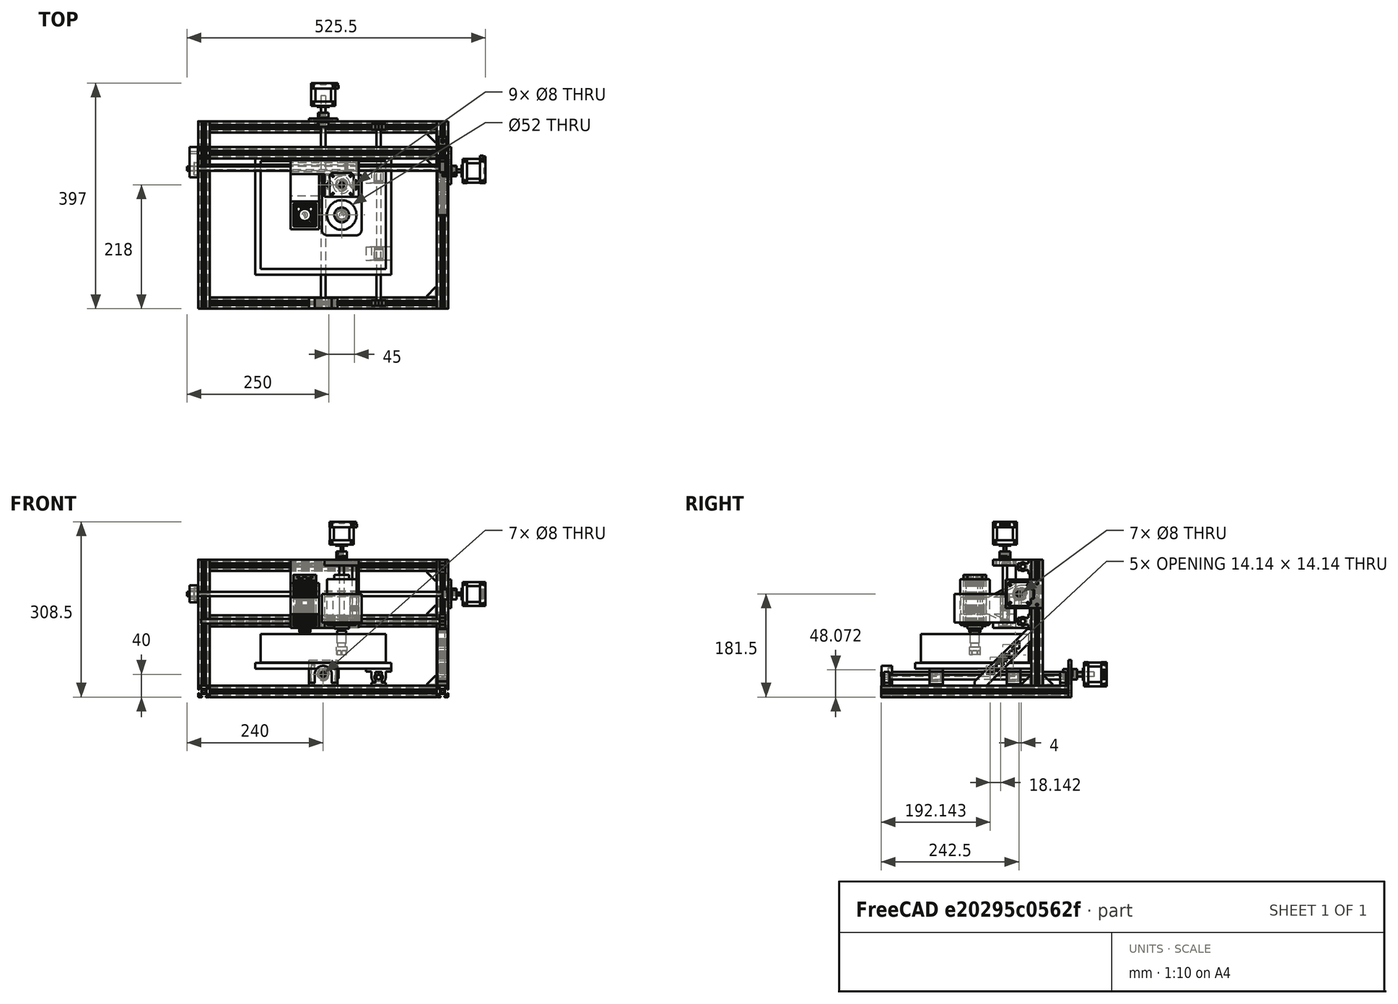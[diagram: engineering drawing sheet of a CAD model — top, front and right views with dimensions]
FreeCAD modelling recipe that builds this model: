
FCSTD DOCUMENT  (FreeCAD 0.16R6706 (Git))
Label: MyCNCparam
License: All rights reserved
LicenseURL: http://en.wikipedia.org/wiki/All_rights_reserved
objects: Part::FeaturePython×60, Sketcher::SketchObject×35, App::DocumentObjectGroup×23, Part::Mirroring×23, PartDesign::Pad×19, PartDesign::Pocket×15, Part::Cylinder×10, Part::Feature×9, Part::MultiFuse×8, Part::Cut×7, Part::Box×7, Part::Compound×5, Part::Fillet×4, Part::Helix×3, Image::ImagePlane×2, Part::Part2DObjectPython×2, PartDesign::Revolution×1, Spreadsheet::Sheet×1, Part::Wedge×1
note: 244 computed .brp shape members not serialized (recipe doc carries the construction recipe); baked Part::Feature solids carry a one-line shape summary decoded from their .brp

FEATURE [Image::ImagePlane] ImagePlane
  XSize = 210
  YSize = 196
FEATURE [Image::ImagePlane] ImagePlane001
  XSize = 20
  YSize = 20
FEATURE [Sketcher::SketchObject] Sketch
  sketch-geometry (17):
    g0: LineSegment StartX=10.27 StartY=3.4 StartZ=0 EndX=9.27 EndY=3.4 EndZ=0
    g1: LineSegment StartX=9.27 StartY=3.4 StartZ=0 EndX=9.27 EndY=3 EndZ=0
    g2: LineSegment StartX=9.27 StartY=3 StartZ=0 EndX=8.37 EndY=3 EndZ=0
    g3: LineSegment StartX=8.37 StartY=3 StartZ=0 EndX=8.37 EndY=5.9 EndZ=0
    g4: LineSegment StartX=8.37 StartY=5.9 StartZ=0 EndX=6.87 EndY=5.9 EndZ=0
    g5: LineSegment StartX=6.87 StartY=5.9 StartZ=0 EndX=4.47 EndY=3.5 EndZ=0
    g6: LineSegment StartX=4.47 StartY=3.5 StartZ=0 EndX=4.47 EndY=0.75 EndZ=0
    g7: LineSegment StartX=4.47 StartY=0.75 StartZ=0 EndX=3.82 EndY=0 EndZ=0
    g8: LineSegment StartX=3.82 StartY=0 StartZ=0 EndX=4.47 EndY=-0.75 EndZ=0
    g9: LineSegment StartX=4.47 StartY=-0.75 StartZ=0 EndX=4.47 EndY=-3.5 EndZ=0
    g10: LineSegment StartX=4.47 StartY=-3.5 StartZ=0 EndX=6.87 EndY=-5.9 EndZ=0
    g11: LineSegment StartX=6.87 StartY=-5.9 StartZ=0 EndX=8.37 EndY=-5.9 EndZ=0
    g12: LineSegment StartX=8.37 StartY=-5.9 StartZ=0 EndX=8.37 EndY=-3 EndZ=0
    g13: LineSegment StartX=8.37 StartY=-3 StartZ=0 EndX=9.27 EndY=-3 EndZ=0
    g14: LineSegment StartX=9.27 StartY=-3 StartZ=0 EndX=9.27 EndY=-3.4 EndZ=0
    g15: LineSegment StartX=9.27 StartY=-3.4 StartZ=0 EndX=10.27 EndY=-3.4 EndZ=0
    g16: LineSegment StartX=10.27 StartY=-3.4 StartZ=0 EndX=10.27 EndY=3.4 EndZ=0
  constraints (48):
    c: Horizontal(g0)
    c: Coincident(g0,g1)
    c: Coincident(g1,g2)
    c: Horizontal(g2)
    c: Coincident(g2,g3)
    c: Vertical(g3)
    c: Coincident(g3,g4)
    c: Coincident(g4,g5)
    c: Coincident(g5,g6)
    c: Vertical(g6)
    c: Coincident(g6,g7)
    c: PointOnObject(g7,g-1)
    c: Coincident(g7,g8)
    c: Coincident(g8,g9)
    c: Vertical(g9)
    c: Coincident(g9,g10)
    c: Coincident(g10,g11)
    c: Horizontal(g11)
    c: Coincident(g11,g12)
    c: Vertical(g12)
    c: Coincident(g12,g13)
    c: Coincident(g13,g14)
    c: Coincident(g14,g15)
    c: Coincident(g15,g16)
    c: Coincident(g16,g0)
    c: Vertical(g16)
    c: Vertical(g1)
    c: Horizontal(g4)
    c: Horizontal(g13)
    c: Vertical(g14)
    c: Horizontal(g15)
    c: Symmetric(g0,g15,g-1)
    c: Symmetric(g13,g1,g-1)
    c: Symmetric(g11,g3,g-1)
    c: Symmetric(g4,g10,g-1)
    c: Symmetric(g5,g9,g-1)
    c: Symmetric(g6,g8,g-1)
    c: DistanceY(g13,g1) = 6
    c: DistanceY(g14,g14) = 0.4
    c: DistanceX(g15,g15) = 1
    c: DistanceX(g13,g13) = 0.9
    c: DistanceY(g12,g12) = 2.9
    c: DistanceX(g11,g11) = 1.5
    c: DistanceX(g7,g6) = 0.65
    c: DistanceY(g8,g6) = 1.5
    c: DistanceY(g9,g9) = 2.75
    c: DistanceX(g-1,g7) = 3.82
    c: Angle(g5,g4) = 2.35619
FEATURE [Sketcher::SketchObject] Sketch001
  sketch-geometry (6):
    g0: LineSegment StartX=-2.88146 StartY=1.89151 StartZ=0 EndX=-1.89151 EndY=2.88146 EndZ=0
    g1: LineSegment StartX=-1.89151 StartY=2.88146 StartZ=0 EndX=2.88146 EndY=-1.89151 EndZ=0
    g2: LineSegment StartX=2.88146 StartY=-1.89151 StartZ=0 EndX=1.89151 EndY=-2.88146 EndZ=0
    g3: LineSegment StartX=1.89151 StartY=-2.88146 StartZ=0 EndX=-2.88146 EndY=1.89151 EndZ=0
    g4: LineSegment [constr] StartX=3.53553 StartY=3.53553 StartZ=0 EndX=0 EndY=0 EndZ=0
    g5: LineSegment [constr] StartX=0 StartY=0 StartZ=0 EndX=3.53553 EndY=-3.53553 EndZ=0
  constraints (17):
    c: Coincident(g0,g1)
    c: Coincident(g1,g2)
    c: Coincident(g2,g3)
    c: Coincident(g3,g0)
    c: Parallel(g3,g1)
    c: Parallel(g0,g2)
    c: Angle(g3,g-1) = 0.785398
    c: Coincident(g4,g-1)
    c: Distance(g4) = 5
    c: Symmetric(g1,g0,g4)
    c: Symmetric(g2,g0,g4)
    c: Distance(g2) = 1.4
    c: Coincident(g5,g-1)
    c: Angle(g5,g4) = 1.5708
    c: Distance(g5) = 5
    c: Symmetric(g2,g1,g5)
    c: Distance(g3) = 6.75
FEATURE [Sketcher::SketchObject] Sketch002
  sketch-geometry (1):
    g0: Circle CenterX=0 CenterY=0 CenterZ=0 NormalX=0 NormalY=0 NormalZ=1 Radius=2.75
  constraints (2):
    c: Coincident(g0,g-1)
    c: Radius(g0) = 2.75
FEATURE [Sketcher::SketchObject] Sketch003
  sketch-geometry (8):
    g0: LineSegment StartX=-8.75 StartY=10 StartZ=0 EndX=8.75 EndY=10 EndZ=0
    g1: LineSegment StartX=10 StartY=8.75 StartZ=0 EndX=10 EndY=-8.75 EndZ=0
    g2: LineSegment StartX=8.75 StartY=-10 StartZ=0 EndX=-8.75 EndY=-10 EndZ=0
    g3: LineSegment StartX=-10 StartY=-8.75 StartZ=0 EndX=-10 EndY=8.75 EndZ=0
    g4: ArcOfCircle CenterX=-8.75 CenterY=8.75 CenterZ=0 NormalX=0 NormalY=0 NormalZ=1 Radius=1.25 StartAngle=1.5708 EndAngle=3.14159
    g5: ArcOfCircle CenterX=8.75 CenterY=8.75 CenterZ=0 NormalX=0 NormalY=0 NormalZ=1 Radius=1.25 StartAngle=4.7348e-08 EndAngle=1.5708
    g6: ArcOfCircle CenterX=8.75 CenterY=-8.75 CenterZ=0 NormalX=0 NormalY=0 NormalZ=1 Radius=1.25 StartAngle=4.71239 EndAngle=6.28319
    g7: ArcOfCircle CenterX=-8.75 CenterY=-8.75 CenterZ=0 NormalX=0 NormalY=0 NormalZ=1 Radius=1.25 StartAngle=3.14159 EndAngle=4.71239
  constraints (27):
    c: Horizontal(g0)
    c: Vertical(g1)
    c: Horizontal(g2)
    c: Vertical(g3)
    c: Coincident(g4,g0)
    c: Coincident(g4,g3)
    c: Tangent(g4,g3)
    c: Tangent(g4,g0)
    c: Coincident(g5,g0)
    c: Coincident(g5,g1)
    c: Tangent(g1,g5)
    c: Tangent(g0,g5)
    c: Coincident(g6,g1)
    c: Coincident(g6,g2)
    c: Tangent(g6,g1)
    c: Tangent(g2,g6)
    c: Coincident(g7,g2)
    c: Coincident(g3,g7)
    c: Tangent(g7,g3)
    c: Tangent(g7,g2)
    c: Symmetric(g3,g3,g-1)
    c: Symmetric(g2,g2,g-2)
    c: Symmetric(g3,g1,g-2)
    c: DistanceX(g3,g1) = 20
    c: DistanceY(g2,g0) = 20
    c: Equal(g7,g4)
    c: Radius(g7) = 1.25
FEATURE [PartDesign::Pad] Pad
  Length = 1
  Length2 = 100
  Sketch = -> Sketch001
  Type = 0
FEATURE [Part::FeaturePython] Clone  label="Clone of Pad"  # Draft clone (typed FeaturePython)
  Objects = -> [Pad]
  Placement = pos=(0,0,0) rot=(0,0,1;1.5708rad)
  Scale = (1,1,1)
FEATURE [PartDesign::Pad] Pad001
  Length = 1
  Length2 = 100
  Sketch = -> Sketch002
  Type = 0
FEATURE [PartDesign::Pad] Pad002
  Length = 1
  Length2 = 100
  Sketch = -> Sketch
  Type = 0
FEATURE [Part::FeaturePython] Array  # Draft array (typed FeaturePython)
  Angle = 360
  ArrayType = 1
  Axis = (0,0,1)
  Base = -> Pad002
  Center = (0,0,0)
  Fuse = false
  IntervalAxis = (0,0,0)
  IntervalX = (1,0,0)
  IntervalY = (0,1,0)
  IntervalZ = (0,0,0)
  NumberPolar = 4
  NumberX = 2
  NumberY = 2
  NumberZ = 1
FEATURE [PartDesign::Pad] Pad003
  Length = 1
  Length2 = 100
  Sketch = -> Sketch003
  Type = 0
FEATURE [Part::MultiFuse] Fusion
  Shapes = -> [Array,Pad001,Clone,Pad]
FEATURE [Part::Cut] Cut  label="20x20ProfileMaster"
  Base = -> Pad003
  Tool = -> Fusion
FEATURE [App::DocumentObjectGroup] Group  label="ImagesReference"
  Group = -> [ImagePlane,ImagePlane001]
FEATURE [Part::FeaturePython] Clone001  label="XProfile1"  # Draft clone (typed FeaturePython)
  Objects = -> [Cut]
  Placement = pos=(-200,10,10) rot=(0,1,0;1.5708rad)
  Scale = (1,1,400)
  expr: Placement.Base.x = -XProfile1.Scale.z / 2
  expr: Scale.z = Spreadsheet.WVX + 180
FEATURE [Part::FeaturePython] Clone002  label="XProfile2"  # Draft clone (typed FeaturePython)
  Objects = -> [Cut]
  Placement = pos=(-200,274.5,10) rot=(0,1,0;1.5708rad)
  Scale = (1,1,400)
  expr: Placement.Base.y = YProfile1.Scale.z / 2 + 109.5
  expr: Placement.Base.x = -XProfile1.Scale.z / 2
  expr: Scale.z = Spreadsheet.WVX + 180
FEATURE [Part::FeaturePython] Clone003  label="YProfile1"  # Draft clone (typed FeaturePython)
  Objects = -> [Cut]
  Placement = pos=(210,0,10) rot=(-1,0,0;1.5708rad)
  Scale = (1,1,330)
  expr: Placement.Base.x = XProfile1.Scale.z / 2 + 10
  expr: Scale.z = Spreadsheet.WVY + 190 - Spreadsheet.Ygap * 2
FEATURE [Part::FeaturePython] Clone004  label="YProfile2"  # Draft clone (typed FeaturePython)
  Objects = -> [Cut]
  Placement = pos=(-210,0,10) rot=(-1,0,0;1.5708rad)
  Scale = (1,1,330)
  expr: Placement.Base.x = -XProfile1.Scale.z / 2 - 10
  expr: Scale.z = Spreadsheet.WVY + 190 - Spreadsheet.Ygap * 2
FEATURE [Part::FeaturePython] Clone005  label="XProfile3"  # Draft clone (typed FeaturePython)
  Objects = -> [Cut]
  Placement = pos=(-200,320,10) rot=(0,1,0;1.5708rad)
  Scale = (1,1,400)
  expr: Placement.Base.y = YProfile1.Scale.z - 10
  expr: Placement.Base.x = -XProfile1.Scale.z / 2
  expr: Scale.z = Spreadsheet.WVX + 180
FEATURE [Sketcher::SketchObject] Sketch004
  Placement = pos=(0,0,0) rot=(0.57735,0.57735,0.57735;2.0944rad)
  sketch-geometry (5):
    g0: LineSegment StartX=0 StartY=0 StartZ=0 EndX=0 EndY=18 EndZ=0
    g1: LineSegment StartX=0 StartY=18 StartZ=0 EndX=2 EndY=18 EndZ=0
    g2: LineSegment StartX=2 StartY=18 StartZ=0 EndX=18 EndY=2 EndZ=0
    g3: LineSegment StartX=18 StartY=2 StartZ=0 EndX=18 EndY=0 EndZ=0
    g4: LineSegment StartX=18 StartY=0 StartZ=0 EndX=0 EndY=0 EndZ=0
  constraints (14):
    c: Coincident(g-1,g0)
    c: PointOnObject(g0,g-2)
    c: Coincident(g0,g1)
    c: Horizontal(g1)
    c: Coincident(g1,g2)
    c: Coincident(g2,g3)
    c: PointOnObject(g3,g-1)
    c: Coincident(g3,g4)
    c: Coincident(g4,g0)
    c: Equal(g4,g0)
    c: Vertical(g3)
    c: DistanceX(g4,g4) = 18
    c: Equal(g1,g3)
    c: DistanceX(g1,g1) = 2
FEATURE [PartDesign::Pad] Pad004
  Length = 18
  Length2 = 100
  Midplane = true
  Placement = pos=(0,0,0) rot=(0.57735,0.57735,0.57735;2.0944rad)
  Sketch = -> Sketch004
  Type = 0
FEATURE [Part::Box] Box  label="Cube"
  Height = 16
  Length = 14
  Placement = pos=(-7,2,2) rot=(0,0,1;0rad)
  Width = 16
FEATURE [Part::Cut] Cut001
  Base = -> Pad004
  Tool = -> Box
FEATURE [Part::Box] Box001  label="Cube001"
  Height = 6
  Length = 4.5
  Placement = pos=(-2.25,-3,9) rot=(0,0,1;0rad)
  Width = 5
FEATURE [Part::FeaturePython] Clone006  label="Clone of Cube001"  # Draft clone (typed FeaturePython)
  Objects = -> [Box001]
  Placement = pos=(-2.25,14,-3) rot=(1,0,0;1.5708rad)
  Scale = (1,1,1)
FEATURE [Part::MultiFuse] Fusion001
  Shapes = -> [Box001,Clone006]
FEATURE [Part::Cut] Cut002  label="45DegUnion"
  Base = -> Cut001
  Tool = -> Fusion001
FEATURE [App::DocumentObjectGroup] Group005  label="AluminiumProfiles"
  Group = -> [Cut]
FEATURE [App::DocumentObjectGroup] Group006  label="Unions"
  Group = -> [Cut002]
FEATURE [Part::FeaturePython] Clone007  label="Clone of 45DegUnion"  # Draft clone (typed FeaturePython)
  Objects = -> [Cut002]
  Placement = pos=(-200,20,10) rot=(0,1,0;1.5708rad)
  Scale = (1,1,1)
  expr: Placement.Base.x = -XProfile1.Scale.z / 2
FEATURE [Part::FeaturePython] Clone008  label="Clone of 45DegUnion001"  # Draft clone (typed FeaturePython)
  Objects = -> [Cut002]
  Placement = pos=(-200,264.5,10) rot=(0.57735,0.57735,-0.57735;2.0944rad)
  Scale = (1,1,1)
  expr: Placement.Base.y = ZProfile1.Placement.Base.y - 10mm
  expr: Placement.Base.x = -XProfile1.Scale.z / 2
FEATURE [Part::FeaturePython] Clone009  label="Clone of 45DegUnion002"  # Draft clone (typed FeaturePython)
  Objects = -> [Cut002]
  Placement = pos=(-200,310,10) rot=(0.57735,0.57735,-0.57735;2.0944rad)
  Scale = (1,1,1)
  expr: Placement.Base.y = YProfile1.Scale.z - 20
  expr: Placement.Base.x = -XProfile1.Scale.z / 2
FEATURE [Part::Mirroring] Part__Mirroring  label="Clone of 45DegUnion (Mirror #1)"
  Base = (0,0,0)
  Normal = (1,0,0)
  Source = -> Clone007
FEATURE [Part::Mirroring] Part__Mirroring001  label="Clone of 45DegUnion001 (Mirror #2)"
  Base = (0,0,0)
  Normal = (1,0,0)
  Source = -> Clone008
FEATURE [Part::Mirroring] Part__Mirroring002  label="Clone of 45DegUnion002 (Mirror #3)"
  Base = (0,0,0)
  Normal = (1,0,0)
  Source = -> Clone009
FEATURE [Part::FeaturePython] Clone010  label="ZProfile1"  # Draft clone (typed FeaturePython)
  Objects = -> [Cut]
  Placement = pos=(-210,274.5,20) rot=(0,0,1;0rad)
  Scale = (1,1,222)
  expr: Scale.z = Spreadsheet.WVZ + 172
  expr: Placement.Base.y = YProfile1.Scale.z / 2 + 109.5
  expr: Placement.Base.x = (XProfile1.Scale.z / 2 + 10) * -1
FEATURE [Part::FeaturePython] Clone011  label="ZProfile2"  # Draft clone (typed FeaturePython)
  Objects = -> [Cut]
  Placement = pos=(210,274.5,20) rot=(0,0,1;0rad)
  Scale = (1,1,222)
  expr: Scale.z = Spreadsheet.WVZ + 172
  expr: Placement.Base.y = YProfile1.Scale.z / 2 + 109.5
  expr: Placement.Base.x = XProfile1.Scale.z / 2 + 10
FEATURE [Part::FeaturePython] Clone012  label="Clone of 45DegUnion003"  # Draft clone (typed FeaturePython)
  Objects = -> [Cut002]
  Placement = pos=(-210,284.5,20) rot=(0,0,1;0rad)
  Scale = (1,1,1)
  expr: Placement.Base.y = ZProfile1.Placement.Base.y + 10mm
  expr: Placement.Base.x = (XProfile1.Scale.z / 2 + 10) * -1
FEATURE [Part::FeaturePython] Clone013  label="Clone of 45DegUnion004"  # Draft clone (typed FeaturePython)
  Objects = -> [Cut002]
  Placement = pos=(-200,274.5,20) rot=(0,0,-1;1.5708rad)
  Scale = (1,1,1)
  expr: Placement.Base.y = ZProfile1.Placement.Base.y
  expr: Placement.Base.x = -XProfile1.Scale.z / 2
FEATURE [Part::FeaturePython] Clone014  label="Clone of 45DegUnion005"  # Draft clone (typed FeaturePython)
  Objects = -> [Cut002]
  Placement = pos=(-210,264.5,20) rot=(0,0,1;3.14159rad)
  Scale = (1,1,1)
  expr: Placement.Base.y = ZProfile1.Placement.Base.y - 10mm
  expr: Placement.Base.x = (XProfile1.Scale.z / 2 + 10) * -1
FEATURE [Part::Mirroring] Part__Mirroring003  label="Clone of 45DegUnion003 (Mirror #4)"
  Base = (0,0,0)
  Normal = (1,0,0)
  Source = -> Clone012
FEATURE [Part::Mirroring] Part__Mirroring004  label="Clone of 45DegUnion004 (Mirror #5)"
  Base = (0,0,0)
  Normal = (1,0,0)
  Source = -> Clone013
FEATURE [Part::Mirroring] Part__Mirroring005  label="Clone of 45DegUnion005 (Mirror #6)"
  Base = (0,0,0)
  Normal = (1,0,0)
  Source = -> Clone014
FEATURE [Part::FeaturePython] Clone015  label="XProfile4"  # Draft clone (typed FeaturePython)
  Objects = -> [Cut]
  Placement = pos=(-200,274.5,232) rot=(0,1,0;1.5708rad)
  Scale = (1,1,400)
  expr: Placement.Base.y = YProfile1.Scale.z / 2 + 109.5
  expr: Placement.Base.x = -XProfile1.Scale.z / 2
  expr: Placement.Base.z = Spreadsheet.WVZ + 182
  expr: Scale.z = Spreadsheet.WVX + 180
FEATURE [Part::FeaturePython] Clone016  label="XProfile5"  # Draft clone (typed FeaturePython)
  Objects = -> [Cut]
  Placement = pos=(-200,274.5,134) rot=(0,1,0;1.5708rad)
  Scale = (1,1,400)
  expr: Placement.Base.y = YProfile1.Scale.z / 2 + 109.5
  expr: Placement.Base.x = -XProfile1.Scale.z / 2
  expr: Scale.z = Spreadsheet.WVX + 180
FEATURE [App::DocumentObjectGroup] Group003  label="Aluminium profiles"
  Group = -> [Clone001,Clone002,Clone003,Clone004,Clone005,Clone010,Clone011,Clone015,Clone016]
FEATURE [Part::FeaturePython] Clone017  label="Clone of 45DegUnion006"  # Draft clone (typed FeaturePython)
  Objects = -> [Cut002]
  Placement = pos=(-200,274.5,222) rot=(0.707107,0.707107,0;3.14159rad)
  Scale = (1,1,1)
  expr: Placement.Base.z = Spreadsheet.WVZ + 172
  expr: Placement.Base.x = XProfile1.Scale.z / 2 * -1
  expr: Placement.Base.y = XProfile4.Placement.Base.y
FEATURE [Part::FeaturePython] Clone018  label="Clone of 45DegUnion007"  # Draft clone (typed FeaturePython)
  Objects = -> [Cut002]
  Placement = pos=(-200,274.5,144) rot=(0,0,-1;1.5708rad)
  Scale = (1,1,1)
  expr: Placement.Base.x = XProfile1.Scale.z / 2 * -1
  expr: Placement.Base.y = XProfile4.Placement.Base.y
FEATURE [Part::Mirroring] Part__Mirroring006  label="Clone of 45DegUnion006 (Mirror #7)"
  Base = (0,0,0)
  Normal = (1,0,0)
  Source = -> Clone017
FEATURE [Part::Mirroring] Part__Mirroring007  label="Clone of 45DegUnion007 (Mirror #8)"
  Base = (0,0,0)
  Normal = (1,0,0)
  Source = -> Clone018
FEATURE [Sketcher::SketchObject] Sketch009
  sketch-geometry (30):
    g0: LineSegment StartX=0 StartY=79.2157 StartZ=0 EndX=79.2157 EndY=0 EndZ=0
    g1: LineSegment StartX=79.2157 StartY=0 StartZ=0 EndX=100 EndY=0 EndZ=0
    g2: LineSegment StartX=100 StartY=0 StartZ=0 EndX=100 EndY=7.5 EndZ=0
    g3: LineSegment StartX=100 StartY=7.5 StartZ=0 EndX=7.5 EndY=100 EndZ=0
    g4: LineSegment StartX=7.5 StartY=100 StartZ=0 EndX=0 EndY=100 EndZ=0
    g5: LineSegment StartX=0 StartY=100 StartZ=0 EndX=0 EndY=79.2157 EndZ=0
    g6: LineSegment StartX=25.0013 StartY=61.2855 StartZ=0 EndX=39.1434 EndY=47.1434 EndZ=0
    g7: LineSegment StartX=39.1434 StartY=47.1434 StartZ=0 EndX=39.1434 EndY=61.2855 EndZ=0
    g8: LineSegment StartX=39.1434 StartY=61.2855 StartZ=0 EndX=25.0013 EndY=61.2855 EndZ=0
    g9: LineSegment StartX=43.1434 StartY=57.2855 StartZ=0 EndX=57.2855 EndY=43.1434 EndZ=0
    g10: LineSegment StartX=43.1434 StartY=43.1434 StartZ=0 EndX=57.2855 EndY=43.1434 EndZ=0
    g11: LineSegment StartX=43.1434 StartY=43.1434 StartZ=0 EndX=43.1434 EndY=57.2855 EndZ=0
    g12: LineSegment StartX=47.1434 StartY=39.1434 StartZ=0 EndX=61.2855 EndY=39.1434 EndZ=0
    g13: LineSegment StartX=61.2855 StartY=39.1434 StartZ=0 EndX=61.2855 EndY=25.0013 EndZ=0
    g14: LineSegment StartX=61.2855 StartY=25.0013 StartZ=0 EndX=47.1434 EndY=39.1434 EndZ=0
    g15: LineSegment StartX=65.2855 StartY=35.1434 StartZ=0 EndX=65.2855 EndY=21.0013 EndZ=0
    g16: LineSegment StartX=65.2855 StartY=21.0013 StartZ=0 EndX=79.4277 EndY=21.0013 EndZ=0
    g17: LineSegment StartX=79.4277 StartY=21.0013 StartZ=0 EndX=65.2855 EndY=35.1434 EndZ=0
    g18: LineSegment [constr] StartX=0 StartY=86.2868 StartZ=0 EndX=86.2868 EndY=0 EndZ=0
    g19: LineSegment [constr] StartX=21.4657 StartY=57.75 StartZ=0 EndX=25.0013 EndY=61.2855 EndZ=0
    g20: LineSegment [constr] StartX=39.1434 StartY=61.2855 StartZ=0 EndX=42.6789 EndY=64.8211 EndZ=0
    g21: LineSegment [constr] StartX=25.0013 StartY=61.2855 StartZ=0 EndX=0 EndY=86.2868 EndZ=0
    g22: LineSegment [constr] StartX=65.2855 StartY=21.0013 StartZ=0 EndX=86.2868 EndY=0 EndZ=0
    g23: LineSegment [constr] StartX=100.429 StartY=0 StartZ=0 EndX=0 EndY=100.429 EndZ=0
    g24: LineSegment [constr] StartX=79.2157 StartY=0 StartZ=0 EndX=93.3579 EndY=14.1421 EndZ=0
    g25: LineSegment StartX=21.0013 StartY=65.2855 StartZ=0 EndX=21.0013 EndY=79.4277 EndZ=0
    g26: LineSegment StartX=21.0013 StartY=79.4277 StartZ=0 EndX=35.1434 EndY=65.2855 EndZ=0
    g27: LineSegment StartX=35.1434 StartY=65.2855 StartZ=0 EndX=21.0013 EndY=65.2855 EndZ=0
    g28: LineSegment [constr] StartX=21.0013 StartY=79.4277 StartZ=0 EndX=0 EndY=100 EndZ=0
    g29: LineSegment [constr] StartX=79.4277 StartY=21.0013 StartZ=0 EndX=100 EndY=0 EndZ=0
  constraints (90):
    c: PointOnObject(g0,g-2)
    c: PointOnObject(g0,g-1)
    c: Coincident(g0,g1)
    c: PointOnObject(g1,g-1)
    c: Coincident(g1,g2)
    c: Coincident(g2,g3)
    c: Coincident(g3,g4)
    c: PointOnObject(g4,g-2)
    c: Horizontal(g4)
    c: Coincident(g4,g5)
    c: Coincident(g5,g0)
    c: Equal(g2,g4)
    c: Equal(g1,g5)
    c: Angle(g0,g-1) = 0.785398
    c: Vertical(g2)
    c: DistanceY(g-1,g4) = 100
    c: Coincident(g6,g7)
    c: Coincident(g7,g8)
    c: Coincident(g8,g6)
    c: Vertical(g7)
    c: Horizontal(g8)
    c: Coincident(g10,g9)
    c: Coincident(g11,g10)
    c: Coincident(g11,g9)
    c: Vertical(g11)
    c: Horizontal(g10)
    c: Horizontal(g12)
    c: Coincident(g12,g13)
    c: Vertical(g13)
    c: Coincident(g13,g14)
    c: Coincident(g14,g12)
    c: Vertical(g15)
    c: Coincident(g15,g16)
    c: Horizontal(g16)
    c: Coincident(g16,g17)
    c: Coincident(g17,g15)
    c: Equal(g15,g16)
    c: Equal(g16,g13)
    c: Equal(g13,g12)
    c: Equal(g12,g10)
    c: Equal(g10,g11)
    c: Equal(g11,g7)
    c: Equal(g7,g8)
    c: DistanceX(g13,g15) = 4
    c: DistanceY(g12,g10) = 4
    c: DistanceX(g6,g10) = 4
    c: Parallel(g18,g0)
    c: PointOnObject(g6,g18)
    c: PointOnObject(g10,g18)
    c: PointOnObject(g13,g18)
    c: PointOnObject(g15,g18)
    c: PointOnObject(g19,g0)
    c: Coincident(g19,g6)
    c: Perpendicular(g0,g19)
    c: Coincident(g20,g7)
    c: PointOnObject(g20,g3)
    c: Perpendicular(g3,g20)
    c: Equal(g19,g20)
    c: Distance(g19) = 5
    c: DistanceX(g4,g4) = 7.5
    c: PointOnObject(g18,g1)
    c: PointOnObject(g18,g5)
    c: Coincident(g21,g6)
    c: Coincident(g21,g18)
    c: Coincident(g22,g15)
    c: Coincident(g22,g18)
    c: PointOnObject(g23,g1)
    c: PointOnObject(g23,g5)
    c: PointOnObject(g7,g23)
    c: PointOnObject(g16,g23)
    c: Coincident(g24,g0)
    c: PointOnObject(g24,g3)
    c: Perpendicular(g3,g24)
    c: Distance(g24) = 20
    c: PointOnObject(g25,g18)
    c: PointOnObject(g25,g23)
    c: Vertical(g25)
    c: Coincident(g25,g26)
    c: PointOnObject(g26,g23)
    c: Coincident(g26,g27)
    c: Coincident(g25,g27)
    c: Horizontal(g27)
    c: DistanceY(g6,g26) = 4
    c: Equal(g8,g27)
    c: Equal(g27,g25)
    c: Coincident(g28,g25)
    c: Coincident(g28,g4)
    c: Coincident(g29,g16)
    c: Coincident(g29,g1)
    c: Equal(g28,g29)
FEATURE [PartDesign::Pad] Pad007  label="45DegreeUnion"
  Length = 18
  Length2 = 100
  Sketch = -> Sketch009
  Type = 0
FEATURE [Part::FeaturePython] Clone020  label="45DegreeUnion002"  # Draft clone (typed FeaturePython)
  Objects = -> [Pad007]
  Placement = pos=(-219,264.5,20) rot=(0.707107,0,0.707107;3.14159rad)
  Scale = (1,1,1)
  expr: Placement.Base.y = XProfile4.Placement.Base.y - 10mm
  expr: Placement.Base.x = (XProfile1.Scale.z / 2 + 19) * -1
FEATURE [Part::Mirroring] Part__Mirroring008  label="45DegreeUnion001"
  Base = (0,0,0)
  Normal = (1,0,0)
  Source = -> Clone020
FEATURE [Sketcher::SketchObject] Sketch010
  Placement = pos=(0,0,0) rot=(0.57735,0.57735,0.57735;2.0944rad)
  sketch-geometry (12):
    g0: ArcOfCircle CenterX=0 CenterY=15 CenterZ=0 NormalX=0 NormalY=0 NormalZ=1 Radius=4 StartAngle=1.63334 EndAngle=7.79144
    g1: LineSegment StartX=0.25 StartY=23.9922 StartZ=0 EndX=6 EndY=23.9922 EndZ=0
    g2: LineSegment StartX=6 StartY=23.9922 StartZ=0 EndX=6 EndY=5 EndZ=0
    g3: LineSegment StartX=6 StartY=5 StartZ=0 EndX=12.5 EndY=5 EndZ=0
    g4: LineSegment StartX=12.5 StartY=5 StartZ=0 EndX=12.5 EndY=0 EndZ=0
    g5: LineSegment StartX=12.5 StartY=0 StartZ=0 EndX=-12.5 EndY=0 EndZ=0
    g6: LineSegment StartX=-12.5 StartY=0 StartZ=0 EndX=-12.5 EndY=5 EndZ=0
    g7: LineSegment StartX=-12.5 StartY=5 StartZ=0 EndX=-6 EndY=5 EndZ=0
    g8: LineSegment StartX=-6 StartY=5 StartZ=0 EndX=-6 EndY=23.9922 EndZ=0
    g9: LineSegment StartX=-6 StartY=23.9922 StartZ=0 EndX=-0.25 EndY=23.9922 EndZ=0
    g10: LineSegment StartX=-0.25 StartY=23.9922 StartZ=0 EndX=-0.25 EndY=18.9922 EndZ=0
    g11: LineSegment StartX=0.25 StartY=23.9922 StartZ=0 EndX=0.25 EndY=18.9922 EndZ=0
  constraints (36):
    c: PointOnObject(g0,g-2)
    c: Symmetric(g0,g0,g-2)
    c: Horizontal(g1)
    c: Coincident(g1,g2)
    c: Vertical(g2)
    c: Coincident(g2,g3)
    c: Horizontal(g3)
    c: Coincident(g3,g4)
    c: PointOnObject(g4,g-1)
    c: Vertical(g4)
    c: Coincident(g4,g5)
    c: PointOnObject(g5,g-1)
    c: Coincident(g5,g6)
    c: Vertical(g6)
    c: Coincident(g6,g7)
    c: Horizontal(g7)
    c: Coincident(g7,g8)
    c: Vertical(g8)
    c: Coincident(g8,g9)
    c: Horizontal(g9)
    c: Coincident(g9,g10)
    c: Coincident(g10,g0)
    c: Vertical(g10)
    c: Coincident(g11,g1)
    c: Coincident(g11,g0)
    c: Vertical(g11)
    c: Symmetric(g1,g8,g-2)
    c: Symmetric(g2,g7,g-2)
    c: Symmetric(g5,g4,g-2)
    c: DistanceX(g9,g1) = 0.5
    c: Radius(g0) = 4
    c: DistanceY(g11,g11) = 5
    c: DistanceX(g8,g1) = 12
    c: DistanceX(g5,g5) = 25
    c: DistanceY(g4,g0) = 15
    c: DistanceY(g6,g6) = 5
FEATURE [PartDesign::Pad] Pad008  label="8mmRodFix"
  Length = 10
  Length2 = 100
  Placement = pos=(0,0,0) rot=(0.57735,0.57735,0.57735;2.0944rad)
  Sketch = -> Sketch010
  Type = 0
FEATURE [Part::FeaturePython] Clone021  label="Clone of Pad008"  # Draft clone (typed FeaturePython)
  Objects = -> [Pad008]
  Placement = pos=(-97.5,5,20) rot=(0,0.707107,0.707107;3.14159rad)
  Scale = (1,1,1)
  expr: Placement.Base.x = (Spreadsheet.WVX / 2 - 12.5) * -1
FEATURE [Part::FeaturePython] Clone022  label="Clone of Pad009"  # Draft clone (typed FeaturePython)
  Objects = -> [Pad008]
  Placement = pos=(-97.5,315,20) rot=(0,0.707107,0.707107;3.14159rad)
  Scale = (1,1,1)
  expr: Placement.Base.y = YProfile1.Scale.z - 15
  expr: Placement.Base.x = (Spreadsheet.WVX / 2 - 12.5) * -1
FEATURE [Part::FeaturePython] Clone023  label="Clone of Pad010"  # Draft clone (typed FeaturePython)
  Objects = -> [Pad008]
  Placement = pos=(-215,264.5,229.5) rot=(0.707107,0,0.707107;3.14159rad)
  Scale = (1,1,1)
  expr: Placement.Base.z = Spreadsheet.WVZ + 179.5
  expr: Placement.Base.y = XProfile4.Placement.Base.y - 10mm
  expr: Placement.Base.x = (XProfile1.Scale.z / 2 + 15) * -1
FEATURE [Part::FeaturePython] Clone024  label="Clone of Pad011"  # Draft clone (typed FeaturePython)
  Objects = -> [Pad008]
  Placement = pos=(-215,264.5,133.5) rot=(0.707107,0,0.707107;3.14159rad)
  Scale = (1,1,1)
  expr: Placement.Base.y = XProfile4.Placement.Base.y - 10mm
  expr: Placement.Base.x = (XProfile1.Scale.z / 2 + 15) * -1
FEATURE [Part::Mirroring] Part__Mirroring010  label="Clone of Pad009 (Mirror #11)"
  Base = (0,0,0)
  Normal = (1,0,0)
  Source = -> Clone022
FEATURE [Part::Mirroring] Part__Mirroring009  label="Clone of Pad008 (Mirror #10)"
  Base = (0,0,0)
  Normal = (1,0,0)
  Source = -> Clone021
FEATURE [Part::Mirroring] Part__Mirroring011  label="Clone of Pad010 (Mirror #12)"
  Base = (0,0,0)
  Normal = (1,0,0)
  Source = -> Clone023
FEATURE [Part::Mirroring] Part__Mirroring012  label="Clone of Pad011 (Mirror #13)"
  Base = (0,0,0)
  Normal = (1,0,0)
  Source = -> Clone024
FEATURE [App::DocumentObjectGroup] Group011  label="RodFix"
  Group = -> [Clone021,Clone022,Clone023,Clone024,Part__Mirroring009,Part__Mirroring010,Part__Mirroring012,Part__Mirroring011]
FEATURE [Part::Cylinder] Cylinder
  Angle = 360
  Height = 320
  Placement = pos=(-97.5,325,35) rot=(1,0,0;1.5708rad)
  Radius = 4
  expr: Height = Spreadsheet.WVY + 180 - Spreadsheet.Ygap * 2
  expr: Placement.Base.x = (Spreadsheet.WVX / 2 - 12.5) * -1
  expr: Placement.Base.y = Spreadsheet.WVY + 185 - Spreadsheet.Ygap * 2
FEATURE [Part::Mirroring] Part__Mirroring013  label="Cylinder (Mirror #14)"
  Base = (0,0,0)
  Normal = (1,0,0)
  Source = -> Cylinder
FEATURE [Part::Cylinder] Cylinder001
  Angle = 360
  Height = 430
  Placement = pos=(-215,249.5,229.5) rot=(0.57735,0.57735,0.57735;2.0944rad)
  Radius = 4
  expr: Placement.Base.z = Spreadsheet.WVZ + 179.5
  expr: Placement.Base.y = XProfile4.Placement.Base.y - 25mm
  expr: Height = XProfile1.Scale.z + 30
  expr: Placement.Base.x = -XProfile1.Scale.z / 2 - 15
FEATURE [Part::FeaturePython] Clone025  label="Clone of Cylinder001"  # Draft clone (typed FeaturePython)
  Objects = -> [Cylinder001]
  Placement = pos=(-215,249.5,133.5) rot=(0.57735,0.57735,0.57735;2.0944rad)
  Scale = (1,1,1)
  expr: Placement.Base.y = XProfile4.Placement.Base.y - 25mm
  expr: Placement.Base.x = -XProfile1.Scale.z / 2 - 15
FEATURE [Part::Feature] Part__Feature  label="Motor-with-connector-final"
  shape: bbox 48 x 42.3 x 60.1 mm, 110 faces (baked)
FEATURE [Sketcher::SketchObject] Sketch011
  sketch-geometry (14):
    g0: LineSegment StartX=-25 StartY=65 StartZ=0 EndX=25 EndY=65 EndZ=0
    g1: LineSegment StartX=25 StartY=65 StartZ=0 EndX=25 EndY=0 EndZ=0
    g2: LineSegment StartX=25 StartY=0 StartZ=0 EndX=-25 EndY=0 EndZ=0
    g3: LineSegment StartX=-25 StartY=0 StartZ=0 EndX=-25 EndY=65 EndZ=0
    g4: Circle CenterX=-18.9188 CenterY=10 CenterZ=0 NormalX=0 NormalY=0 NormalZ=1 Radius=2
    g5: Circle CenterX=18.9188 CenterY=10 CenterZ=0 NormalX=0 NormalY=0 NormalZ=1 Radius=2
    g6: Circle CenterX=0 CenterY=40 CenterZ=0 NormalX=0 NormalY=0 NormalZ=1 Radius=11
    g7: Circle CenterX=-15.5 CenterY=55.5 CenterZ=0 NormalX=0 NormalY=0 NormalZ=1 Radius=1.5
    g8: Circle CenterX=-15.5 CenterY=24.5 CenterZ=0 NormalX=0 NormalY=0 NormalZ=1 Radius=1.5
    g9: Circle CenterX=15.5 CenterY=24.5 CenterZ=0 NormalX=0 NormalY=0 NormalZ=1 Radius=1.5
    g10: Circle CenterX=15.5 CenterY=55.5 CenterZ=0 NormalX=0 NormalY=0 NormalZ=1 Radius=1.5
    g11: LineSegment [constr] StartX=-25 StartY=40 StartZ=0 EndX=25 EndY=40 EndZ=0
    g12: LineSegment [constr] StartX=-15.5 StartY=55.5 StartZ=0 EndX=15.5 EndY=55.5 EndZ=0
    g13: LineSegment [constr] StartX=-15.5 StartY=55.5 StartZ=0 EndX=-15.5 EndY=24.5 EndZ=0
  constraints (36):
    c: Coincident(g0,g1)
    c: Coincident(g1,g2)
    c: Coincident(g2,g3)
    c: Coincident(g3,g0)
    c: Horizontal(g0)
    c: Horizontal(g2)
    c: Vertical(g1)
    c: Vertical(g3)
    c: PointOnObject(g1,g-1)
    c: Symmetric(g1,g2,g-2)
    c: PointOnObject(g6,g-2)
    c: PointOnObject(g6,g11)
    c: PointOnObject(g11,g1)
    c: PointOnObject(g11,g3)
    c: Symmetric(g8,g7,g11)
    c: Symmetric(g9,g10,g11)
    c: Symmetric(g10,g7,g-2)
    c: Symmetric(g8,g9,g-2)
    c: Equal(g7,g8)
    c: Equal(g8,g10)
    c: Equal(g10,g9)
    c: Radius(g7) = 1.5
    c: Coincident(g12,g7)
    c: Coincident(g12,g10)
    c: Coincident(g13,g7)
    c: Coincident(g13,g8)
    c: Equal(g13,g12)
    c: Symmetric(g5,g4,g-2)
    c: Equal(g5,g4)
    c: Radius(g4) = 2
    c: DistanceY(g2,g4) = 10
    c: DistanceY(g-1,g6) = 40
    c: DistanceX(g12,g12) = 31
    c: Radius(g6) = 11
    c: DistanceX(g0,g0) = 50
    c: DistanceY(g3,g3) = 65
FEATURE [PartDesign::Pad] Pad009  label="MotorFixing"
  Length = 5
  Length2 = 100
  Sketch = -> Sketch011
  Type = 0
FEATURE [Part::FeaturePython] Clone026  label="Clone of MotorFixing001"  # Draft clone (typed FeaturePython)
  Objects = -> [Pad009]
  Placement = pos=(0,335,0) rot=(1,0,0;1.5708rad)
  Scale = (1,1,1)
  expr: Placement.Base.y = YProfile1.Scale.z + 5
FEATURE [Part::FeaturePython] Clone027  label="Clone of MotorFixing"  # Draft clone (typed FeaturePython)
  Objects = -> [Pad009]
  Placement = pos=(220,284.5,181.5) rot=(0.707107,0,0.707107;3.14159rad)
  Scale = (1,1,1)
  expr: Placement.Base.z = Spreadsheet.WVZ / 2 + 156.5
  expr: Placement.Base.x = XProfile1.Scale.z / 2 + 20
  expr: Placement.Base.y = XProfile4.Placement.Base.y + 10mm
FEATURE [Part::FeaturePython] Clone028  label="Clone of Motor-with-connector-final"  # Draft clone (typed FeaturePython)
  Objects = -> [Part__Feature]
  Placement = pos=(0,397,40) rot=(1,0,0;1.5708rad)
  Scale = (1,1,1)
  expr: Placement.Base.y = YProfile1.Scale.z + 67
FEATURE [Part::FeaturePython] Clone029  label="Clone of Motor-with-connector-final001"  # Draft clone (typed FeaturePython)
  Objects = -> [Part__Feature]
  Placement = pos=(285.5,242.5,181.5) rot=(0.57735,0.57735,-0.57735;4.18879rad)
  Scale = (1,1,1)
  expr: Placement.Base.z = Spreadsheet.WVZ / 2 + 156.5
  expr: Placement.Base.x = XProfile1.Scale.z / 2 + 85.5
  expr: Placement.Base.y = XProfile4.Placement.Base.y - 32mm
FEATURE [Part::Feature] Part__Feature001  label="coupling-compound"
  shape: bbox 3.9 x 6.2 x 3.9 mm, 12 faces (baked)
FEATURE [Part::Feature] Part__Feature002  label="coupling-compound001"
  shape: bbox 7.092 x 5.717 x 3.9 mm, 12 faces (baked)
FEATURE [Part::Feature] Part__Feature003  label="coupling-compound002"
  shape: bbox 4.973 x 6.792 x 3.9 mm, 12 faces (baked)
FEATURE [Part::Feature] Part__Feature004  label="coupling-compound003"
  shape: bbox 7.22 x 6.433 x 3.9 mm, 12 faces (baked)
FEATURE [Part::Feature] Part__Feature005  label="coupling-compound004"
  shape: bbox 28.44 x 28.71 x 24.7 mm, 28 faces (baked)
FEATURE [Part::Compound] Compound  label="CouplingMotor"
  Links = -> [Part__Feature005,Part__Feature001,Part__Feature002,Part__Feature003,Part__Feature004]
FEATURE [App::DocumentObjectGroup] Group013  label="Motors"
  Group = -> [Part__Feature,Pad009,Compound]
FEATURE [Part::FeaturePython] Clone030  label="Clone of CouplingMotor"  # Draft clone (typed FeaturePython)
  Objects = -> [Compound]
  Placement = pos=(0,320,40) rot=(-1,0,0;1.5708rad)
  Scale = (1,1,1)
  expr: Placement.Base.y = YProfile1.Scale.z - 10
FEATURE [Part::FeaturePython] Clone031  label="Clone of CouplingMotor001"  # Draft clone (typed FeaturePython)
  Objects = -> [Compound]
  Placement = pos=(210,242.5,181.5) rot=(0,1,0;1.5708rad)
  Scale = (1,1,1)
  expr: Placement.Base.z = Spreadsheet.WVZ / 2 + 156.5
  expr: Placement.Base.x = XProfile1.Scale.z / 2 + 10
  expr: Placement.Base.y = XProfile4.Placement.Base.y - 32mm
FEATURE [Part::Cylinder] Cylinder002
  Angle = 360
  Height = 116
  Radius = 4
  expr: Height = Spreadsheet.WVZ + 66
FEATURE [Part::Helix] Helix
  Angle = 0
  Height = 116
  LocalCoord = 0
  Pitch = 3
  Radius = 4
  Style = 1
  expr: Height = Spreadsheet.WVZ + 66
FEATURE [Part::Compound] Compound001  label="ThreadedRod-8x75mm"
  Links = -> [Helix,Cylinder002]
  Placement = pos=(32.5,218,239.5) rot=(0,1,0;3.14159rad)
  expr: Placement.Base.z = 189.5 + Spreadsheet.WVZ
  expr: Placement.Base.y = XProfile4.Placement.Base.y - 56.5mm
FEATURE [Part::Cylinder] Cylinder003
  Angle = 360
  Height = 460
  Radius = 4
  expr: Height = XProfile4.Scale.z + 60
FEATURE [Part::Helix] Helix001
  Angle = 0
  Height = 460
  LocalCoord = 0
  Pitch = 3
  Radius = 4
  Style = 1
  expr: Height = XProfile4.Scale.z + 60
FEATURE [Part::Compound] Compound002  label="ThreadedRod-8x410mm"
  Links = -> [Helix001,Cylinder003]
  Placement = pos=(220,246.5,181.5) rot=(0,-1,0;1.5708rad)
  expr: Placement.Base.z = Spreadsheet.WVZ / 2 + 156.5
  expr: Placement.Base.x = XProfile1.Scale.z / 2 + 20
  expr: Placement.Base.y = XProfile4.Placement.Base.y - 28mm
FEATURE [Part::Feature] Part__Feature006  label="608ZZ_Ball_Bearing"
  shape: bbox 22 x 22 x 7 mm, 14 faces (baked)
FEATURE [Part::FeaturePython] Clone032  label="Clone of 608ZZ_Ball_Bearing"  # Draft clone (typed FeaturePython)
  Objects = -> [Part__Feature006]
  Placement = pos=(0,15.5,40) rot=(1,0,0;1.5708rad)
  Scale = (1,1,1)
FEATURE [Part::FeaturePython] Clone033  label="Clone of 608ZZ_Ball_Bearing001"  # Draft clone (typed FeaturePython)
  Objects = -> [Part__Feature006]
  Placement = pos=(-224,246.5,181.5) rot=(0.57735,0.57735,0.57735;2.0944rad)
  Scale = (1,1,1)
  expr: Placement.Base.z = Spreadsheet.WVZ / 2 + 156.5
  expr: Placement.Base.y = XProfile4.Placement.Base.y - 28mm
  expr: Placement.Base.x = (XProfile1.Scale.z / 2 + 24) * -1
FEATURE [Sketcher::SketchObject] Sketch012
  sketch-geometry (9):
    g0: ArcOfCircle CenterX=0 CenterY=20 CenterZ=0 NormalX=0 NormalY=0 NormalZ=1 Radius=15 StartAngle=0 EndAngle=3.14159
    g1: LineSegment StartX=-15 StartY=20 StartZ=0 EndX=-15 EndY=5 EndZ=0
    g2: LineSegment StartX=-15 StartY=5 StartZ=0 EndX=-25 EndY=5 EndZ=0
    g3: LineSegment StartX=-25 StartY=5 StartZ=0 EndX=-25 EndY=0 EndZ=0
    g4: LineSegment StartX=-25 StartY=0 StartZ=0 EndX=25 EndY=0 EndZ=0
    g5: LineSegment StartX=25 StartY=0 StartZ=0 EndX=25 EndY=5 EndZ=0
    g6: LineSegment StartX=25 StartY=5 StartZ=0 EndX=15 EndY=5 EndZ=0
    g7: LineSegment StartX=15 StartY=5 StartZ=0 EndX=15 EndY=20 EndZ=0
    g8: Circle CenterX=0 CenterY=20 CenterZ=0 NormalX=0 NormalY=0 NormalZ=1 Radius=4.5
  constraints (26):
    c: PointOnObject(g0,g-2)
    c: Tangent(g0,g1) = -1.5708
    c: Coincident(g1,g2)
    c: Horizontal(g2)
    c: Coincident(g2,g3)
    c: PointOnObject(g3,g-1)
    c: Vertical(g3)
    c: Coincident(g3,g4)
    c: PointOnObject(g4,g-1)
    c: Coincident(g4,g5)
    c: Coincident(g5,g6)
    c: Coincident(g6,g7)
    c: Coincident(g7,g0)
    c: Vertical(g7)
    c: Horizontal(g6)
    c: Symmetric(g0,g0,g-2)
    c: Vertical(g1)
    c: Symmetric(g2,g5,g-2)
    c: Vertical(g5)
    c: Symmetric(g1,g6,g-2)
    c: Radius(g8) = 4.5
    c: DistanceY(g3,g3) = 5
    c: DistanceX(g4,g4) = 50
    c: Radius(g0) = 15
    c: DistanceY(g1,g1) = 15
    c: Coincident(g0,g8)
FEATURE [PartDesign::Pad] Pad010  label="BearingFixBef"
  Length = 18
  Length2 = 100
  Midplane = true
  Sketch = -> Sketch012
  Type = 0
FEATURE [Sketcher::SketchObject] Sketch013
  ExternalGeometry = -> [Pad010]
  Placement = pos=(0,0,-9) rot=(1,0,0;3.14159rad)
  Support = -> Pad010 [Face10]
  sketch-geometry (1):
    g0: Circle CenterX=0 CenterY=-20 CenterZ=0 NormalX=0 NormalY=0 NormalZ=1 Radius=11
  constraints (2):
    c: Coincident(g0,g-3)
    c: Radius(g0) = 11
FEATURE [PartDesign::Pocket] Pocket  label="BearingFix"
  Length = 7
  Sketch = -> Sketch013
  Type = 0
FEATURE [Part::FeaturePython] Clone035  label="Clone of BearingFixA"  # Draft clone (typed FeaturePython)
  Objects = -> [Pocket]
  Placement = pos=(0,10,20) rot=(1,0,0;1.5708rad)
  Scale = (1,1,1)
FEATURE [Sketcher::SketchObject] Sketch014
  sketch-geometry (7):
    g0: ArcOfCircle CenterX=0 CenterY=38 CenterZ=0 NormalX=0 NormalY=0 NormalZ=1 Radius=15 StartAngle=0 EndAngle=3.14159
    g1: LineSegment StartX=-15 StartY=38 StartZ=0 EndX=-15 EndY=0 EndZ=0
    g2: LineSegment StartX=-15 StartY=0 StartZ=0 EndX=15 EndY=0 EndZ=0
    g3: LineSegment StartX=15 StartY=0 StartZ=0 EndX=15 EndY=38 EndZ=0
    g4: Circle CenterX=0 CenterY=38 CenterZ=0 NormalX=0 NormalY=0 NormalZ=1 Radius=4.5
    g5: Circle CenterX=-7.5 CenterY=10 CenterZ=0 NormalX=0 NormalY=0 NormalZ=1 Radius=2
    g6: Circle CenterX=7.5 CenterY=10 CenterZ=0 NormalX=0 NormalY=0 NormalZ=1 Radius=2
  constraints (20):
    c: PointOnObject(g0,g-2)
    c: Tangent(g0,g1) = -1.5708
    c: PointOnObject(g2,g-1)
    c: PointOnObject(g2,g-1)
    c: Coincident(g3,g0)
    c: Vertical(g3)
    c: Symmetric(g0,g0,g-2)
    c: Vertical(g1)
    c: Symmetric(g1,g3,g-2)
    c: Radius(g4) = 4.5
    c: Radius(g0) = 15
    c: DistanceY(g1,g1) = 38
    c: Coincident(g0,g4)
    c: Coincident(g1,g2)
    c: Equal(g5,g6)
    c: Symmetric(g5,g6,g-2)
    c: Radius(g5) = 2
    c: DistanceX(g5,g6) = 15
    c: DistanceY(g1,g5) = 10
    c: DistanceX(g2,g2) = 30
FEATURE [PartDesign::Pad] Pad011  label="BearingFixBefB"
  Length = 15
  Length2 = 100
  Midplane = true
  Sketch = -> Sketch014
  Type = 0
FEATURE [Sketcher::SketchObject] Sketch015
  ExternalGeometry = -> [Pad011]
  Placement = pos=(0,0,7.5) rot=(0,0,1;0rad)
  Support = -> Pad011 [Face9]
  sketch-geometry (1):
    g0: Circle CenterX=0 CenterY=38 CenterZ=0 NormalX=0 NormalY=0 NormalZ=1 Radius=11
  constraints (2):
    c: Coincident(g0,g-3)
    c: Radius(g0) = 11
FEATURE [PartDesign::Pocket] Pocket001  label="BearingFixB"
  Length = 7
  Sketch = -> Sketch015
  Type = 0
FEATURE [Part::FeaturePython] Clone036  label="BearingFixB001"  # Draft clone (typed FeaturePython)
  Objects = -> [Pocket001]
  Placement = pos=(-228,284.5,181.5) rot=(0.707107,0,0.707107;3.14159rad)
  Scale = (1,1,1)
  expr: Placement.Base.z = Spreadsheet.WVZ / 2 + 156.5
  expr: Placement.Base.y = XProfile4.Placement.Base.y + 10mm
  expr: Placement.Base.x = (XProfile1.Scale.z / 2 + 28) * -1
FEATURE [Part::Feature] Part__Feature007  label="LM8uu001"
  shape: bbox 15 x 15 x 24 mm, 20 faces (baked)
FEATURE [Part::FeaturePython] Clone037  label="Clone of LM8uu001"  # Draft clone (typed FeaturePython)
  Objects = -> [Part__Feature007]
  Placement = pos=(-97.5,97,35) rot=(1,0,0;1.5708rad)
  Scale = (1,1,1)
  expr: Placement.Base.y = YProfile1.Scale.z / 2 - (Spreadsheet.WVY + 20) / 2 + 12 + Spreadsheet.Ygap
  expr: Placement.Base.x = (Spreadsheet.WVX / 2 - 12.5) * -1
FEATURE [Part::FeaturePython] Clone038  label="Clone of LM8uu002"  # Draft clone (typed FeaturePython)
  Objects = -> [Part__Feature007]
  Placement = pos=(-97.5,233,35) rot=(1,0,0;1.5708rad)
  Scale = (1,1,1)
  expr: Placement.Base.y = YProfile1.Scale.z / 2 + (Spreadsheet.WVY + 20) / 2 - 12 - Spreadsheet.Ygap
  expr: Placement.Base.x = (Spreadsheet.WVX / 2 - 12.5) * -1
FEATURE [Part::FeaturePython] Clone039  label="Clone of LM8uu003"  # Draft clone (typed FeaturePython)
  Objects = -> [Part__Feature007]
  Placement = pos=(-45.5,249.5,229.5) rot=(0,1,0;1.5708rad)
  Scale = (1,1,1)
  expr: Placement.Base.z = Spreadsheet.WVZ + 179.5
  expr: Placement.Base.y = XProfile4.Placement.Base.y - 25mm
FEATURE [Part::FeaturePython] Clone040  label="Clone of LM8uu004"  # Draft clone (typed FeaturePython)
  Objects = -> [Part__Feature007]
  Placement = pos=(-45.5,249.5,133.5) rot=(0,1,0;1.5708rad)
  Scale = (1,1,1)
  expr: Placement.Base.y = XProfile4.Placement.Base.y - 25mm
FEATURE [Part::Mirroring] Part__Mirroring014  label="Clone of LM8uu001 (Mirror #15)"
  Base = (0,0,0)
  Normal = (1,0,0)
  Source = -> Clone037
FEATURE [Part::Mirroring] Part__Mirroring015  label="Clone of LM8uu002 (Mirror #16)"
  Base = (0,0,0)
  Normal = (1,0,0)
  Source = -> Clone038
FEATURE [Part::Mirroring] Part__Mirroring016  label="Clone of LM8uu003 (Mirror #17)"
  Base = (0,0,0)
  Normal = (1,0,0)
  Placement = pos=(5,0,0) rot=(0,0,1;0rad)
  Source = -> Clone039
FEATURE [Part::Mirroring] Part__Mirroring017  label="Clone of LM8uu004 (Mirror #18)"
  Base = (0,0,0)
  Normal = (1,0,0)
  Placement = pos=(5,0,0) rot=(0,0,1;0rad)
  Source = -> Clone040
FEATURE [Sketcher::SketchObject] Sketch016
  Placement = pos=(0,0,0) rot=(1,0,0;1.5708rad)
  sketch-geometry (9):
    g0: LineSegment StartX=22.5 StartY=0 StartZ=0 EndX=22.5 EndY=5 EndZ=0
    g1: LineSegment StartX=22.5 StartY=5 StartZ=0 EndX=12.5 EndY=5 EndZ=0
    g2: LineSegment StartX=22.5 StartY=0 StartZ=0 EndX=-22.5 EndY=0 EndZ=0
    g3: LineSegment StartX=-22.5 StartY=0 StartZ=0 EndX=-22.5 EndY=5 EndZ=0
    g4: LineSegment StartX=-22.5 StartY=5 StartZ=0 EndX=-12.5 EndY=5 EndZ=0
    g5: LineSegment StartX=-12.5 StartY=5 StartZ=0 EndX=-12.5 EndY=15 EndZ=0
    g6: LineSegment StartX=12.5 StartY=5 StartZ=0 EndX=12.5 EndY=15 EndZ=0
    g7: ArcOfCircle CenterX=0 CenterY=15 CenterZ=0 NormalX=0 NormalY=0 NormalZ=1 Radius=12.5 StartAngle=6.28318 EndAngle=9.42478
    g8: Circle CenterX=0 CenterY=15 CenterZ=0 NormalX=0 NormalY=0 NormalZ=1 Radius=7.5
  constraints (26):
    c: Vertical(g0)
    c: Coincident(g0,g1)
    c: Horizontal(g1)
    c: Coincident(g0,g2)
    c: PointOnObject(g2,g-1)
    c: Horizontal(g2)
    c: Coincident(g2,g3)
    c: Vertical(g3)
    c: Coincident(g3,g4)
    c: Horizontal(g4)
    c: Coincident(g4,g5)
    c: Vertical(g5)
    c: Coincident(g6,g1)
    c: Vertical(g6)
    c: PointOnObject(g7,g-2)
    c: Coincident(g7,g5)
    c: Coincident(g7,g6)
    c: Tangent(g5,g7)
    c: Tangent(g7,g6)
    c: Symmetric(g0,g3,g-2)
    c: Radius(g7) = 12.5
    c: Coincident(g8,g7)
    c: Radius(g8) = 7.5
    c: DistanceY(g0,g0) = 5
    c: DistanceX(g1,g1) = 10
    c: DistanceY(g-1,g7) = 15
FEATURE [PartDesign::Pad] Pad012  label="LM8UUBearingFix"
  Length = 24
  Length2 = 100
  Midplane = true
  Placement = pos=(0,0,0) rot=(1,0,0;1.5708rad)
  Sketch = -> Sketch016
  Type = 0
FEATURE [App::DocumentObjectGroup] Group016  label="Bearing001"
  Group = -> [Part__Feature006,Pad010,Pocket,Pad011,Pocket001,Part__Feature007,Pad012]
FEATURE [Part::FeaturePython] Clone041  label="Clone of LM8UUBearingFix"  # Draft clone (typed FeaturePython)
  Objects = -> [Pad012]
  Placement = pos=(-97.5,97,50) rot=(0,0.707107,-0.707107;3.14159rad)
  Scale = (1,1,1)
  expr: Placement.Base.x = (Spreadsheet.WVX / 2 - 12.5) * -1
  expr: Placement.Base.y = YProfile1.Scale.z / 2 - (Spreadsheet.WVY + 20) / 2 + 12 + Spreadsheet.Ygap
FEATURE [Part::FeaturePython] Clone042  label="Clone of LM8UUBearingFix001"  # Draft clone (typed FeaturePython)
  Objects = -> [Pad012]
  Placement = pos=(-97.5,233,50) rot=(0,0.707107,-0.707107;3.14159rad)
  Scale = (1,1,1)
  expr: Placement.Base.x = (Spreadsheet.WVX / 2 - 12.5) * -1
  expr: Placement.Base.y = YProfile1.Scale.z / 2 + (Spreadsheet.WVY + 20) / 2 - 12 - Spreadsheet.Ygap
FEATURE [Part::Mirroring] Part__Mirroring018  label="Clone of LM8UUBearingFix (Mirror #19)"
  Base = (0,0,0)
  Normal = (1,0,0)
  Source = -> Clone041
FEATURE [Part::Mirroring] Part__Mirroring019  label="Clone of LM8UUBearingFix001 (Mirror #20)"
  Base = (0,0,0)
  Normal = (1,0,0)
  Source = -> Clone042
FEATURE [Sketcher::SketchObject] Sketch017
  Placement = pos=(0,0,0) rot=(0.57735,0.57735,0.57735;2.0944rad)
  sketch-geometry (12):
    g0: LineSegment StartX=0 StartY=0 StartZ=0 EndX=0 EndY=79 EndZ=0
    g1: LineSegment StartX=0 StartY=79 StartZ=0 EndX=65 EndY=79 EndZ=0
    g2: LineSegment StartX=65 StartY=79 StartZ=0 EndX=65 EndY=69 EndZ=0
    g3: LineSegment StartX=65 StartY=69 StartZ=0 EndX=25 EndY=69 EndZ=0
    g4: LineSegment StartX=25 StartY=69 StartZ=0 EndX=25 EndY=10 EndZ=0
    g5: LineSegment StartX=25 StartY=10 StartZ=0 EndX=65 EndY=10 EndZ=0
    g6: LineSegment StartX=65 StartY=10 StartZ=0 EndX=65 EndY=0 EndZ=0
    g7: LineSegment StartX=65 StartY=0 StartZ=0 EndX=0 EndY=0 EndZ=0
    g8: Circle CenterX=12 CenterY=67 CenterZ=0 NormalX=0 NormalY=0 NormalZ=1 Radius=7.5
    g9: Circle CenterX=12 CenterY=12 CenterZ=0 NormalX=0 NormalY=0 NormalZ=1 Radius=7.5
    g10: LineSegment [constr] StartX=12 StartY=67 StartZ=0 EndX=12 EndY=12 EndZ=0
    g11: Circle CenterX=15 CenterY=39.5 CenterZ=0 NormalX=0 NormalY=0 NormalZ=1 Radius=5
  constraints (34):
    c: Coincident(g-1,g0)
    c: Vertical(g0)
    c: Coincident(g0,g1)
    c: Horizontal(g1)
    c: Coincident(g1,g2)
    c: Vertical(g2)
    c: Coincident(g2,g3)
    c: Horizontal(g3)
    c: Coincident(g3,g4)
    c: Vertical(g4)
    c: Coincident(g4,g5)
    c: Horizontal(g5)
    c: Coincident(g5,g6)
    c: PointOnObject(g6,g-1)
    c: Coincident(g6,g7)
    c: Coincident(g7,g0)
    c: Vertical(g6)
    c: Equal(g5,g3)
    c: Equal(g8,g9)
    c: Radius(g8) = 7.5
    c: Coincident(g10,g8)
    c: Coincident(g10,g9)
    c: Vertical(g10)
    c: DistanceY(g10,g10) = 55
    c: DistanceX(g-1,g9) = 12
    c: DistanceY(g-1,g9) = 12
    c: DistanceY(g8,g0) = 12
    c: DistanceY(g2,g2) = 10
    c: DistanceY(g6,g6) = 10
    c: DistanceX(g1,g1) = 65
    c: DistanceX(g0,g3) = 25
    c: DistanceX(g8,g11) = 3
    c: DistanceY(g11,g8) = 27.5
    c: Radius(g11) = 5
FEATURE [PartDesign::Pad] Pad013
  Length = 60
  Length2 = 100
  Midplane = true
  Placement = pos=(0,0,0) rot=(0.57735,0.57735,0.57735;2.0944rad)
  Sketch = -> Sketch017
  Type = 0
FEATURE [Sketcher::SketchObject] Sketch018
  Placement = pos=(0,0,79) rot=(0,0,-1;1.5708rad)
  Support = -> Pad013 [Face2]
  sketch-geometry (8):
    g0: Circle CenterX=-44 CenterY=0 CenterZ=0 NormalX=0 NormalY=0 NormalZ=1 Radius=11
    g1: Circle CenterX=-59.5 CenterY=15.5 CenterZ=0 NormalX=0 NormalY=0 NormalZ=1 Radius=1.5
    g2: Circle CenterX=-28.5 CenterY=15.5 CenterZ=0 NormalX=0 NormalY=0 NormalZ=1 Radius=1.5
    g3: Circle CenterX=-59.5 CenterY=-15.5 CenterZ=0 NormalX=0 NormalY=0 NormalZ=1 Radius=1.5
    g4: Circle CenterX=-28.5 CenterY=-15.5 CenterZ=0 NormalX=0 NormalY=0 NormalZ=1 Radius=1.5
    g5: LineSegment [constr] StartX=-44 StartY=22.5 StartZ=0 EndX=-44 EndY=-22.5 EndZ=0
    g6: Circle CenterX=-44 CenterY=-22.5 CenterZ=0 NormalX=0 NormalY=0 NormalZ=1 Radius=4
    g7: Circle CenterX=-44 CenterY=22.5 CenterZ=0 NormalX=0 NormalY=0 NormalZ=1 Radius=4
  constraints (20):
    c: PointOnObject(g0,g-1)
    c: Equal(g4,g3)
    c: Equal(g3,g1)
    c: Equal(g1,g2)
    c: Radius(g2) = 1.5
    c: Radius(g0) = 11
    c: Vertical(g5)
    c: PointOnObject(g0,g5)
    c: Symmetric(g5,g5,g-1)
    c: DistanceY(g5,g5) = 45
    c: Symmetric(g1,g3,g-1)
    c: Symmetric(g4,g2,g-1)
    c: Symmetric(g3,g4,g5)
    c: DistanceY(g3,g1) = 31
    c: DistanceX(g1,g2) = 31
    c: DistanceX(g0,g-1) = 44
    c: Equal(g7,g6)
    c: Radius(g6) = 4
    c: Symmetric(g6,g7,g-1)
    c: Coincident(g6,g5)
FEATURE [PartDesign::Pocket] Pocket002
  Length = 12
  Placement = pos=(0,0,0) rot=(0.57735,0.57735,0.57735;2.0944rad)
  Sketch = -> Sketch018
  Type = 0
FEATURE [Sketcher::SketchObject] Sketch019
  Placement = pos=(0,0,10) rot=(0,0,-1;1.5708rad)
  Support = -> Pocket002 [Face17]
  sketch-geometry (4):
    g0: Circle CenterX=-44 CenterY=0 CenterZ=0 NormalX=0 NormalY=0 NormalZ=1 Radius=11
    g1: Circle CenterX=-44 CenterY=22.5 CenterZ=0 NormalX=0 NormalY=0 NormalZ=1 Radius=4
    g2: Circle CenterX=-44 CenterY=-22.5 CenterZ=0 NormalX=0 NormalY=0 NormalZ=1 Radius=4
    g3: LineSegment [constr] StartX=-44 StartY=22.5 StartZ=0 EndX=-44 EndY=-22.5 EndZ=0
  constraints (11):
    c: PointOnObject(g0,g-1)
    c: Radius(g0) = 11
    c: Equal(g1,g2)
    c: Radius(g1) = 4
    c: Coincident(g3,g1)
    c: Coincident(g3,g2)
    c: Vertical(g3)
    c: PointOnObject(g0,g3)
    c: DistanceX(g0,g-1) = 44
    c: DistanceY(g3,g3) = 45
    c: Symmetric(g2,g1,g-1)
FEATURE [PartDesign::Pocket] Pocket003
  Length = 7
  Placement = pos=(0,0,0) rot=(0.57735,0.57735,0.57735;2.0944rad)
  Sketch = -> Sketch019
  Type = 0
FEATURE [Part::FeaturePython] Clone045  label="Clone of CouplingMotor002"  # Draft clone (typed FeaturePython)
  Objects = -> [Compound]
  Placement = pos=(32.5,218,231.5) rot=(0,0,1;0rad)
  Scale = (1,1,1)
  expr: Placement.Base.z = 181.5 + Spreadsheet.WVZ
  expr: Placement.Base.y = XProfile4.Placement.Base.y - 56.5mm
FEATURE [Part::FeaturePython] Clone046  label="Clone of Motor-with-connector-final002"  # Draft clone (typed FeaturePython)
  Objects = -> [Part__Feature]
  Placement = pos=(32.5,218,308.5) rot=(1,0,0;3.14159rad)
  Scale = (1,1,1)
  expr: Placement.Base.z = 258.5 + Spreadsheet.WVZ
  expr: Placement.Base.y = XProfile4.Placement.Base.y - 56.5mm
FEATURE [App::DocumentObjectGroup] Group014  label="Motors&Fix&Coupl"
  Group = -> [Clone026,Clone027,Clone028,Clone029,Clone030,Clone031,Clone046,Clone045]
FEATURE [Part::Cylinder] Cylinder004  label="Rod8x74mm"
  Angle = 360
  Height = 115
  Placement = pos=(10,218,126.5) rot=(0,0,1;0rad)
  Radius = 4
  expr: Height = Spreadsheet.WVZ + 65
  expr: Placement.Base.y = XProfile4.Placement.Base.y - 56.5mm
FEATURE [Part::FeaturePython] Clone047  label="Rod8x74mm001"  # Draft clone (typed FeaturePython)
  Objects = -> [Cylinder004]
  Placement = pos=(55,218,126.5) rot=(0,0,1;0rad)
  Scale = (1,1,1)
  expr: Placement.Base.y = XProfile4.Placement.Base.y - 56.5mm
FEATURE [Part::FeaturePython] Clone048  label="Clone of 608ZZ_Ball_Bearing002"  # Draft clone (typed FeaturePython)
  Objects = -> [Part__Feature006]
  Placement = pos=(32.5,218,128) rot=(0,0,1;0rad)
  Scale = (1,1,1)
  expr: Placement.Base.y = XProfile4.Placement.Base.y - 56.5mm
FEATURE [Sketcher::SketchObject] Sketch020
  ExternalGeometry = -> [Pocket003]
  Placement = pos=(0,0,69) rot=(0.707107,0.707107,0;3.14159rad)
  Support = -> Pocket003 [Face15]
  sketch-geometry (4):
    g0: Circle CenterX=28.5 CenterY=15.5 CenterZ=0 NormalX=0 NormalY=0 NormalZ=1 Radius=2.5
    g1: Circle CenterX=59.5 CenterY=15.5 CenterZ=0 NormalX=0 NormalY=0 NormalZ=1 Radius=2.5
    g2: Circle CenterX=28.5 CenterY=-15.5 CenterZ=0 NormalX=0 NormalY=0 NormalZ=1 Radius=2.5
    g3: Circle CenterX=59.5 CenterY=-15.5 CenterZ=0 NormalX=0 NormalY=0 NormalZ=1 Radius=2.5
  constraints (8):
    c: Coincident(g0,g-3)
    c: Coincident(g1,g-4)
    c: Coincident(g2,g-6)
    c: Coincident(g3,g-5)
    c: Equal(g3,g2)
    c: Equal(g2,g1)
    c: Equal(g1,g0)
    c: Radius(g0) = 2.5
FEATURE [PartDesign::Pocket] Pocket004
  Length = 5
  Placement = pos=(0,0,0) rot=(0.57735,0.57735,0.57735;2.0944rad)
  Sketch = -> Sketch020
  Type = 0
FEATURE [Sketcher::SketchObject] Sketch021
  ExternalGeometry = -> [Pocket004]
  Placement = pos=(0,0,3) rot=(0,0,-1;1.5708rad)
  Support = -> Pocket004 [Face33]
  sketch-geometry (1):
    g0: Circle CenterX=-44 CenterY=0 CenterZ=0 NormalX=0 NormalY=0 NormalZ=1 Radius=7
  constraints (2):
    c: Coincident(g0,g-3)
    c: Radius(g0) = 7
FEATURE [PartDesign::Pocket] Pocket005  label="Carriage001"
  Length = 5
  Placement = pos=(0,0,0) rot=(0.57735,0.57735,0.57735;2.0944rad)
  Sketch = -> Sketch021
  Type = 0
FEATURE [App::DocumentObjectGroup] Group017  label="Carriage"
  Group = -> [Pocket002,Pocket003,Pad013,Pocket004,Pocket005]
FEATURE [Part::Cylinder] Cylinder005
  Angle = 360
  Height = 375
  Radius = 4
  expr: Height = Spreadsheet.WVY + 185
FEATURE [Part::Helix] Helix002
  Angle = 0
  Height = 375
  LocalCoord = 0
  Pitch = 3
  Radius = 4
  Style = 1
  expr: Height = Spreadsheet.WVY + 185
FEATURE [Part::Compound] Compound003  label="ThreadedRod-8x300mm001"
  Links = -> [Helix002,Cylinder005]
  Placement = pos=(0,375,40) rot=(1,0,0;1.5708rad)
  expr: Placement.Base.y = Spreadsheet.WVY + 185
FEATURE [App::DocumentObjectGroup] Group012  label="8mmRods"
  Group = -> [Part__Mirroring013,Clone025,Cylinder001,Compound002,Compound001,Cylinder004,Clone047,Compound003]
FEATURE [Sketcher::SketchObject] Sketch022
  sketch-geometry (10):
    g0: Circle CenterX=-22.5 CenterY=0 CenterZ=0 NormalX=0 NormalY=0 NormalZ=1 Radius=7.5
    g1: Circle CenterX=22.5 CenterY=0 CenterZ=0 NormalX=0 NormalY=0 NormalZ=1 Radius=7.5
    g2: Circle CenterX=0 CenterY=0 CenterZ=0 NormalX=0 NormalY=0 NormalZ=1 Radius=4.5
    g3: LineSegment StartX=-35 StartY=-79 StartZ=0 EndX=-35 EndY=17 EndZ=0
    g4: LineSegment StartX=-35 StartY=17 StartZ=0 EndX=35 EndY=17 EndZ=0
    g5: LineSegment StartX=35 StartY=17 StartZ=0 EndX=35 EndY=-79 EndZ=0
    g6: Circle CenterX=0 CenterY=-53 CenterZ=0 NormalX=0 NormalY=0 NormalZ=1 Radius=26
    g7: LineSegment StartX=-25 StartY=-89 StartZ=0 EndX=25 EndY=-89 EndZ=0
    g8: ArcOfCircle CenterX=-25 CenterY=-79 CenterZ=0 NormalX=0 NormalY=0 NormalZ=1 Radius=10 StartAngle=3.14159 EndAngle=4.71239
    g9: ArcOfCircle CenterX=25 CenterY=-79 CenterZ=0 NormalX=0 NormalY=0 NormalZ=1 Radius=10 StartAngle=4.71239 EndAngle=6.28319
  constraints (31):
    c: PointOnObject(g0,g-1)
    c: PointOnObject(g1,g-1)
    c: Coincident(g2,g-1)
    c: Symmetric(g1,g0,g-2)
    c: Radius(g2) = 4.5
    c: Radius(g0) = 7.5
    c: Equal(g0,g1)
    c: DistanceX(g0,g1) = 45
    c: Vertical(g3)
    c: Coincident(g3,g4)
    c: Horizontal(g4)
    c: Coincident(g4,g5)
    c: Vertical(g5)
    c: PointOnObject(g6,g-2)
    c: Radius(g6) = 26
    c: DistanceY(g0,g3) = 17
    c: DistanceX(g3,g0) = 12.5
    c: Symmetric(g4,g3,g-2)
    c: Horizontal(g7)
    c: Coincident(g8,g3)
    c: Coincident(g8,g7)
    c: Coincident(g9,g5)
    c: Coincident(g9,g7)
    c: Equal(g9,g8)
    c: Tangent(g8,g7)
    c: Tangent(g8,g3)
    c: Tangent(g7,g9)
    c: Tangent(g9,g5)
    c: Radius(g9) = 10
    c: DistanceY(g6,g4) = 70
    c: DistanceY(g7,g6) = 36
FEATURE [PartDesign::Pad] Pad014  label="SpindleFix"
  Length = 50
  Length2 = 100
  Sketch = -> Sketch022
  Type = 0
FEATURE [Part::FeaturePython] Clone050  label="Clone of SpindleFix"  # Draft clone (typed FeaturePython)
  Objects = -> [Pad014]
  Placement = pos=(32.5,218,131.5) rot=(0,0,1;0rad)
  Scale = (1,1,1)
  expr: Placement.Base.y = XProfile4.Placement.Base.y - 56.5mm
FEATURE [App::DocumentObjectGroup] Group007  label="ProfileUnions"
  Group = -> [Part__Mirroring,Part__Mirroring001,Part__Mirroring002,Part__Mirroring003,Part__Mirroring004,Part__Mirroring005,Part__Mirroring006,Part__Mirroring007,Clone050]
FEATURE [Part::FeaturePython] Clone051  label="Clone of LM8uu005"  # Draft clone (typed FeaturePython)
  Objects = -> [Part__Feature007]
  Placement = pos=(10,218,168.5) rot=(0,0,1;0rad)
  Scale = (1,1,1)
  expr: Placement.Base.y = XProfile4.Placement.Base.y - 56.5mm
FEATURE [Part::FeaturePython] Clone052  label="Clone of LM8uu006"  # Draft clone (typed FeaturePython)
  Objects = -> [Part__Feature007]
  Placement = pos=(10,218,144.5) rot=(0,0,1;0rad)
  Scale = (1,1,1)
  expr: Placement.Base.y = XProfile4.Placement.Base.y - 56.5mm
FEATURE [Part::Mirroring] Part__Mirroring020  label="Clone of LM8uu005 (Mirror #21)"
  Base = (32.52,0,0)
  Normal = (1,0,0)
  Source = -> Clone051
FEATURE [Part::Mirroring] Part__Mirroring021  label="Clone of LM8uu006 (Mirror #22)"
  Base = (32.52,0,0)
  Normal = (1,0,0)
  Source = -> Clone052
FEATURE [App::DocumentObjectGroup] Group015  label="Bearing"
  Group = -> [Clone032,Clone033,Clone035,Clone036,Part__Mirroring014,Part__Mirroring015,Part__Mirroring016,Part__Mirroring017,Part__Mirroring018,Part__Mirroring019,Part__Mirroring021,Part__Mirroring020]
FEATURE [Sketcher::SketchObject] Sketch023
  sketch-geometry (16):
    g0: LineSegment StartX=0 StartY=0 StartZ=0 EndX=9.5 EndY=0 EndZ=0
    g1: LineSegment StartX=9.5 StartY=0 StartZ=0 EndX=9.5 EndY=13 EndZ=0
    g2: LineSegment StartX=9.5 StartY=13 StartZ=0 EndX=6.9 EndY=13 EndZ=0
    g3: LineSegment StartX=6.9 StartY=13 StartZ=0 EndX=6.9 EndY=20 EndZ=0
    g4: LineSegment StartX=6.9 StartY=20 StartZ=0 EndX=8 EndY=20 EndZ=0
    g5: LineSegment StartX=8 StartY=20 StartZ=0 EndX=8 EndY=41.5 EndZ=0
    g6: LineSegment StartX=8 StartY=41.5 StartZ=0 EndX=4 EndY=41.5 EndZ=0
    g7: LineSegment StartX=4 StartY=41.5 StartZ=0 EndX=4 EndY=45.5 EndZ=0
    g8: LineSegment StartX=4 StartY=45.5 StartZ=0 EndX=13 EndY=45.5 EndZ=0
    g9: LineSegment StartX=13 StartY=45.5 StartZ=0 EndX=13 EndY=52 EndZ=0
    g10: LineSegment StartX=13 StartY=52 StartZ=0 EndX=26 EndY=52 EndZ=0
    g11: LineSegment StartX=26 StartY=52 StartZ=0 EndX=26 EndY=132.5 EndZ=0
    g12: LineSegment StartX=13 StartY=140 StartZ=0 EndX=0 EndY=140 EndZ=0
    g13: LineSegment StartX=26 StartY=132.5 StartZ=0 EndX=13 EndY=132.5 EndZ=0
    g14: LineSegment StartX=13 StartY=132.5 StartZ=0 EndX=13 EndY=140 EndZ=0
    g15: LineSegment StartX=0 StartY=140 StartZ=0 EndX=0 EndY=0 EndZ=0
  constraints (47):
    c: Coincident(g-1,g0)
    c: PointOnObject(g0,g-1)
    c: Coincident(g0,g1)
    c: Vertical(g1)
    c: Coincident(g1,g2)
    c: Coincident(g2,g3)
    c: Vertical(g3)
    c: Coincident(g3,g4)
    c: Horizontal(g4)
    c: Coincident(g4,g5)
    c: Vertical(g5)
    c: Coincident(g5,g6)
    c: Horizontal(g6)
    c: Coincident(g6,g7)
    c: Vertical(g7)
    c: Coincident(g7,g8)
    c: Horizontal(g8)
    c: Coincident(g8,g9)
    c: Vertical(g9)
    c: Coincident(g9,g10)
    c: Horizontal(g10)
    c: Vertical(g11)
    c: PointOnObject(g12,g-2)
    c: Horizontal(g12)
    c: Horizontal(g2)
    c: DistanceX(g0,g0) = 9.5
    c: DistanceX(g-1,g2) = 6.9
    c: DistanceX(g-1,g4) = 8
    c: DistanceX(g-1,g6) = 4
    c: DistanceX(g-1,g8) = 13
    c: DistanceX(g-1,g11) = 26
    c: DistanceY(g1,g1) = 13
    c: DistanceY(g3,g3) = 7
    c: DistanceY(g5,g5) = 21.5
    c: DistanceY(g7,g7) = 4
    c: Horizontal(g13)
    c: Coincident(g14,g13)
    c: Vertical(g14)
    c: Coincident(g14,g12)
    c: DistanceX(g12,g12) = 13
    c: DistanceY(g9,g9) = 6.5
    c: DistanceY(g14,g14) = 7.5
    c: Coincident(g11,g10)
    c: Coincident(g13,g11)
    c: DistanceY(g11,g11) = 80.5
    c: Coincident(g15,g12)
    c: Coincident(g15,g-1)
FEATURE [PartDesign::Revolution] Revolution  label="SpindleRev"
  Angle = 360
  Axis = (0,1,0)
  Base = (0,0,0)
  ReferenceAxis = -> Sketch023 [V_Axis]
  Reversed = true
  Sketch = -> Sketch023
FEATURE [Sketcher::SketchObject] Sketch024
  Placement = pos=(0,0,0) rot=(1,0,0;1.5708rad)
  Support = -> Revolution [Face1]
  sketch-geometry (8):
    g0: LineSegment StartX=0 StartY=10 StartZ=0 EndX=-8.66025 EndY=5 EndZ=0
    g1: LineSegment StartX=-8.66025 StartY=5 StartZ=0 EndX=-8.66025 EndY=-5 EndZ=0
    g2: LineSegment StartX=-8.66025 StartY=-5 StartZ=0 EndX=0 EndY=-10 EndZ=0
    g3: LineSegment StartX=0 StartY=-10 StartZ=0 EndX=8.66025 EndY=-5 EndZ=0
    g4: LineSegment StartX=8.66025 StartY=-5 StartZ=0 EndX=8.66025 EndY=5 EndZ=0
    g5: LineSegment StartX=8.66025 StartY=5 StartZ=0 EndX=0 EndY=10 EndZ=0
    g6: Circle [constr] CenterX=0 CenterY=0 CenterZ=0 NormalX=0 NormalY=0 NormalZ=1 Radius=10
    g7: Circle CenterX=0 CenterY=0 CenterZ=0 NormalX=0 NormalY=0 NormalZ=1 Radius=12
  constraints (18):
    c: Coincident(g0,g1)
    c: Coincident(g1,g2)
    c: Coincident(g2,g3)
    c: Coincident(g3,g4)
    c: Coincident(g4,g5)
    c: Coincident(g5,g0)
    c: Equal(g0, g1-g5) x5
    c: PointOnObject(g0,g6)
    c: PointOnObject(g1,g6)
    c: PointOnObject(g2,g6)
    c: PointOnObject(g3,g6)
    c: PointOnObject(g4,g6)
    c: PointOnObject(g5,g6)
    c: Coincident(g6,g-1)
    c: PointOnObject(g0,g-2)
    c: Radius(g6) = 10
    c: Coincident(g7,g-1)
    c: Radius(g7) = 12
FEATURE [PartDesign::Pocket] Pocket006
  Length = 7
  Sketch = -> Sketch024
  Type = 0
FEATURE [Part::Fillet] Fillet
  Base = -> Pocket006
  Edges = 2 edges r=2: [Edge52,Edge53]
FEATURE [Part::Fillet] Fillet001  label="Spindle"
  Base = -> Fillet
  Edges = 4 edges r=1: [Edge5,Edge15,Edge16,Edge20]
FEATURE [Part::FeaturePython] Clone053  label="Clone of Spindle"  # Draft clone (typed FeaturePython)
  Objects = -> [Fillet001]
  Placement = pos=(32.5,165,75) rot=(1,0,0;1.5708rad)
  Scale = (1,1,1)
  expr: Placement.Base.y = XProfile4.Placement.Base.y - 109.5mm
FEATURE [App::DocumentObjectGroup] Group018  label="Spindle001"
  Group = -> [Revolution,Fillet001]
FEATURE [Part::Box] Box002  label="Cube002"
  Height = 80
  Length = 40
  Placement = pos=(-20,-20,10) rot=(0,0,1;0rad)
  Width = 40
FEATURE [Part::Cylinder] Cylinder006
  Angle = 360
  Height = 10
  Radius = 5
FEATURE [Part::Cylinder] Cylinder007
  Angle = 360
  Height = 7
  Radius = 10
FEATURE [Part::MultiFuse] Fusion002
  Shapes = -> [Cylinder007,Cylinder006,Box002]
FEATURE [Part::Box] Box003  label="Cube003"
  Height = 80
  Length = 10
  Placement = pos=(17,-15.5,10) rot=(0,0,1;0rad)
  Width = 2.5
FEATURE [Part::FeaturePython] Clone054  label="Clone of Cube002"  # Draft clone (typed FeaturePython)
  Objects = -> [Box003]
  Placement = pos=(15,-11.5,10) rot=(0,0,1;0rad)
  Scale = (1,1,1)
FEATURE [Part::FeaturePython] Clone055  label="Clone of Cube003"  # Draft clone (typed FeaturePython)
  Objects = -> [Box003]
  Placement = pos=(12,-7.5,10) rot=(0,0,1;0rad)
  Scale = (1,1,1)
FEATURE [Part::FeaturePython] Clone056  label="Clone of Cube004"  # Draft clone (typed FeaturePython)
  Objects = -> [Box003]
  Placement = pos=(10,-3.5,10) rot=(0,0,1;0rad)
  Scale = (1,1,1)
FEATURE [Part::MultiFuse] Fusion003
  Shapes = -> [Clone056,Clone055,Clone054,Box003]
FEATURE [Part::Mirroring] Part__Mirroring022  label="Fusion001 (Mirror #1)"
  Base = (0,0,0)
  Normal = (0,1,0)
  Source = -> Fusion003
FEATURE [Part::MultiFuse] Fusion004
  Shapes = -> [Fusion003,Part__Mirroring022]
FEATURE [Part::FeaturePython] Array001  # Draft array (typed FeaturePython)
  Angle = 360
  ArrayType = 1
  Axis = (0,0,1)
  Base = -> Fusion004
  Center = (0,0,0)
  Fuse = false
  IntervalAxis = (0,0,0)
  IntervalX = (1,0,0)
  IntervalY = (0,1,0)
  IntervalZ = (0,0,0)
  NumberPolar = 4
  NumberX = 4
  NumberY = 2
  NumberZ = 1
FEATURE [Part::Cut] Cut003
  Base = -> Fusion002
  Tool = -> Array001
FEATURE [Part::Cylinder] Cylinder008
  Angle = 360
  Height = 7
  Placement = pos=(10,0,0) rot=(0,0,1;0rad)
  Radius = 0.25
FEATURE [Part::FeaturePython] Array002  # Draft array (typed FeaturePython)
  Angle = 360
  ArrayType = 1
  Axis = (0,0,1)
  Base = -> Cylinder008
  Center = (0,0,0)
  Fuse = false
  IntervalAxis = (0,0,0)
  IntervalX = (1,0,0)
  IntervalY = (0,1,0)
  IntervalZ = (0,0,0)
  NumberPolar = 65
  NumberX = 2
  NumberY = 2
  NumberZ = 1
FEATURE [Part::Cut] Cut004
  Base = -> Cut003
  Tool = -> Array002
FEATURE [Part::Cylinder] Cylinder009
  Angle = 360
  Height = 10
  Radius = 2
FEATURE [Part::Cut] Cut005  label="Laser"
  Base = -> Cut004
  Tool = -> Cylinder009
FEATURE [Part::Feature] Part__Feature008  label="fan-40x40mm-final"
  Placement = pos=(0,0,90) rot=(0,0,1;0rad)
  shape: bbox 40 x 40 x 10 mm, 172 faces (baked)
FEATURE [Part::Compound] Compound004  label="LaserComp"
  Links = -> [Part__Feature008,Cut005]
FEATURE [App::DocumentObjectGroup] Group020  label="Laser001"
  Group = -> [Compound004]
FEATURE [Part::FeaturePython] Clone057  label="Clone of LaserComp"  # Draft clone (typed FeaturePython)
  Objects = -> [Compound004]
  Placement = pos=(-32.5,165,115) rot=(0,0,1;0rad)
  Scale = (1,1,1)
  expr: Placement.Base.y = XProfile4.Placement.Base.y - 109.5mm
FEATURE [Sketcher::SketchObject] Sketch025
  Placement = pos=(0,0,0) rot=(1,0,0;1.5708rad)
  sketch-geometry (9):
    g0: LineSegment StartX=0 StartY=0 StartZ=0 EndX=25 EndY=0 EndZ=0
    g1: LineSegment StartX=25 StartY=0 StartZ=0 EndX=25 EndY=79 EndZ=0
    g2: LineSegment StartX=25 StartY=79 StartZ=0 EndX=0 EndY=79 EndZ=0
    g3: LineSegment StartX=0 StartY=79 StartZ=0 EndX=0 EndY=0 EndZ=0
    g4: Circle CenterX=12.5 CenterY=12 CenterZ=0 NormalX=0 NormalY=0 NormalZ=1 Radius=7.5
    g5: Circle CenterX=12.5 CenterY=67 CenterZ=0 NormalX=0 NormalY=0 NormalZ=1 Radius=7.5
    g6: Circle CenterX=15.5 CenterY=39.5 CenterZ=0 NormalX=0 NormalY=0 NormalZ=1 Radius=5
    g7: LineSegment [constr] StartX=12.5 StartY=67 StartZ=0 EndX=12.5 EndY=12 EndZ=0
    g8: LineSegment [constr] StartX=15.5 StartY=39.5 StartZ=0 EndX=12.5 EndY=39.5 EndZ=0
  constraints (25):
    c: Coincident(g0,g1)
    c: Coincident(g1,g2)
    c: Coincident(g2,g3)
    c: Coincident(g3,g0)
    c: Horizontal(g0)
    c: Horizontal(g2)
    c: Vertical(g1)
    c: Vertical(g3)
    c: Coincident(g0,g-1)
    c: Equal(g5,g4)
    c: Coincident(g7,g5)
    c: Coincident(g7,g4)
    c: Vertical(g7)
    c: Radius(g4) = 7.5
    c: Coincident(g8,g6)
    c: PointOnObject(g8,g7)
    c: Horizontal(g8)
    c: Symmetric(g4,g5,g8)
    c: DistanceX(g8,g8) = 3
    c: Radius(g6) = 5
    c: DistanceY(g7,g7) = 55
    c: DistanceY(g3,g3) = 79
    c: DistanceX(g0,g0) = 25
    c: DistanceX(g-1,g4) = 12.5
    c: DistanceY(g-1,g8) = 39.5
FEATURE [PartDesign::Pad] Pad015
  Length = 120
  Length2 = 100
  Placement = pos=(0,0,0) rot=(1,0,0;1.5708rad)
  Sketch = -> Sketch025
  Type = 0
FEATURE [Sketcher::SketchObject] Sketch026
  ExternalGeometry = -> [Pad015]
  Placement = pos=(25,0,0) rot=(0.707107,0,0.707107;3.14159rad)
  Support = -> Pad015 [Face2]
  sketch-geometry (6):
    g0: LineSegment StartX=24.5 StartY=0 StartZ=0 EndX=54.5 EndY=0 EndZ=0
    g1: LineSegment StartX=54.5 StartY=0 StartZ=0 EndX=54.5 EndY=50 EndZ=0
    g2: LineSegment StartX=54.5 StartY=50 StartZ=0 EndX=24.5 EndY=50 EndZ=0
    g3: LineSegment StartX=24.5 StartY=50 StartZ=0 EndX=24.5 EndY=0 EndZ=0
    g4: LineSegment [constr] StartX=0 StartY=0 StartZ=0 EndX=24.5 EndY=0 EndZ=0
    g5: LineSegment [constr] StartX=79 StartY=0 StartZ=0 EndX=54.5 EndY=0 EndZ=0
  constraints (16):
    c: Coincident(g0,g1)
    c: Coincident(g1,g2)
    c: Coincident(g2,g3)
    c: Coincident(g3,g0)
    c: Horizontal(g0)
    c: Horizontal(g2)
    c: Vertical(g1)
    c: Vertical(g3)
    c: DistanceY(g1,g1) = 50
    c: DistanceX(g2,g2) = 30
    c: Coincident(g4,g-1)
    c: Coincident(g4,g0)
    c: Coincident(g5,g-3)
    c: Horizontal(g5)
    c: Coincident(g5,g0)
    c: Equal(g4,g5)
FEATURE [PartDesign::Pad] Pad016
  Length = 97
  Length2 = 100
  Placement = pos=(0,0,0) rot=(1,0,0;1.5708rad)
  Sketch = -> Sketch026
  Type = 0
FEATURE [Sketcher::SketchObject] Sketch027
  ExternalGeometry = -> [Pad016]
  Placement = pos=(25,0,0) rot=(0.707107,0,0.707107;3.14159rad)
  Support = -> Pad016 [Face3]
  sketch-geometry (8):
    g0: LineSegment StartX=0 StartY=120 StartZ=0 EndX=10 EndY=120 EndZ=0
    g1: LineSegment StartX=10 StartY=120 StartZ=0 EndX=10 EndY=60 EndZ=0
    g2: LineSegment StartX=10 StartY=60 StartZ=0 EndX=0 EndY=60 EndZ=0
    g3: LineSegment StartX=0 StartY=60 StartZ=0 EndX=0 EndY=120 EndZ=0
    g4: LineSegment StartX=79 StartY=120 StartZ=0 EndX=69 EndY=120 EndZ=0
    g5: LineSegment StartX=69 StartY=120 StartZ=0 EndX=69 EndY=60 EndZ=0
    g6: LineSegment StartX=69 StartY=60 StartZ=0 EndX=79 EndY=60 EndZ=0
    g7: LineSegment StartX=79 StartY=60 StartZ=0 EndX=79 EndY=120 EndZ=0
  constraints (22):
    c: Coincident(g0,g1)
    c: Coincident(g1,g2)
    c: Coincident(g2,g3)
    c: Coincident(g3,g0)
    c: Horizontal(g0)
    c: Horizontal(g2)
    c: Vertical(g1)
    c: Vertical(g3)
    c: Coincident(g0,g-4)
    c: Coincident(g4,g5)
    c: Coincident(g5,g6)
    c: Coincident(g6,g7)
    c: Coincident(g7,g4)
    c: Horizontal(g4)
    c: Horizontal(g6)
    c: Vertical(g5)
    c: Vertical(g7)
    c: Coincident(g4,g-3)
    c: Equal(g2,g6)
    c: DistanceX(g2,g2) = 10
    c: DistanceY(g1,g1) = 60
    c: Equal(g1,g5)
FEATURE [PartDesign::Pad] Pad017
  Length = 40
  Length2 = 100
  Placement = pos=(0,0,0) rot=(1,0,0;1.5708rad)
  Sketch = -> Sketch027
  Type = 0
FEATURE [Sketcher::SketchObject] Sketch028
  ExternalGeometry = -> [Pad017]
  Placement = pos=(0,0,0) rot=(1,0,0;3.14159rad)
  Support = -> Pad017 [Face18]
  sketch-geometry (11):
    g0: Circle CenterX=44 CenterY=90 CenterZ=0 NormalX=0 NormalY=0 NormalZ=1 Radius=15
    g1: Circle CenterX=44 CenterY=112.5 CenterZ=0 NormalX=0 NormalY=0 NormalZ=1 Radius=4
    g2: Circle CenterX=44 CenterY=67.5 CenterZ=0 NormalX=0 NormalY=0 NormalZ=1 Radius=4
    g3: Circle CenterX=59.5 CenterY=74.5 CenterZ=0 NormalX=0 NormalY=0 NormalZ=1 Radius=1.5
    g4: Circle CenterX=59.5 CenterY=105.5 CenterZ=0 NormalX=0 NormalY=0 NormalZ=1 Radius=1.5
    g5: Circle CenterX=28.5 CenterY=105.5 CenterZ=0 NormalX=0 NormalY=0 NormalZ=1 Radius=1.5
    g6: Circle CenterX=28.5 CenterY=74.5 CenterZ=0 NormalX=0 NormalY=0 NormalZ=1 Radius=1.5
    g7: LineSegment [constr] StartX=44 StartY=90 StartZ=0 EndX=0 EndY=90 EndZ=0
    g8: LineSegment [constr] StartX=44 StartY=112.5 StartZ=0 EndX=44 EndY=67.5 EndZ=0
    g9: LineSegment [constr] StartX=44 StartY=90 StartZ=0 EndX=44 EndY=120 EndZ=0
    g10: LineSegment [constr] StartX=44 StartY=90 StartZ=0 EndX=44 EndY=60 EndZ=0
  constraints (31):
    c: Coincident(g7,g0)
    c: PointOnObject(g7,g-3)
    c: Horizontal(g7)
    c: DistanceX(g7,g7) = 44
    c: Coincident(g8,g2)
    c: Vertical(g8)
    c: Coincident(g1,g8)
    c: PointOnObject(g0,g8)
    c: Symmetric(g1,g2,g7)
    c: PointOnObject(g9,g7)
    c: PointOnObject(g9,g-4)
    c: Vertical(g9)
    c: Coincident(g10,g9)
    c: PointOnObject(g10,g-5)
    c: Vertical(g10)
    c: Equal(g9,g10)
    c: Symmetric(g5,g4,g8)
    c: Symmetric(g5,g6,g7)
    c: Symmetric(g4,g3,g7)
    c: Symmetric(g3,g6,g8)
    c: Equal(g3,g6)
    c: Equal(g6,g5)
    c: Equal(g5,g4)
    c: Radius(g4) = 1.5
    c: DistanceY(g3,g4) = 31
    c: DistanceX(g6,g3) = 31
    c: Radius(g0) = 15
    c: Equal(g1,g2)
    c: Radius(g1) = 4
    c: Coincident(g9,g0)
    c: DistanceY(g2,g1) = 45
FEATURE [PartDesign::Pocket] Pocket007
  Length = 10
  Placement = pos=(0,0,0) rot=(1,0,0;1.5708rad)
  Sketch = -> Sketch028
  Type = 0
FEATURE [Sketcher::SketchObject] Sketch029
  ExternalGeometry = -> [Pocket007]
  Placement = pos=(0,0,69) rot=(1,0,0;3.14159rad)
  Support = -> Pocket007 [Face25]
  sketch-geometry (7):
    g0: Circle CenterX=44 CenterY=90 CenterZ=0 NormalX=0 NormalY=0 NormalZ=1 Radius=11
    g1: Circle CenterX=44 CenterY=112.5 CenterZ=0 NormalX=0 NormalY=0 NormalZ=1 Radius=4
    g2: Circle CenterX=44 CenterY=67.5 CenterZ=0 NormalX=0 NormalY=0 NormalZ=1 Radius=4
    g3: LineSegment [constr] StartX=44 StartY=67.5 StartZ=0 EndX=44 EndY=112.5 EndZ=0
    g4: LineSegment [constr] StartX=0 StartY=90 StartZ=0 EndX=44 EndY=90 EndZ=0
    g5: LineSegment [constr] StartX=44 StartY=90 StartZ=0 EndX=44 EndY=60 EndZ=0
    g6: LineSegment [constr] StartX=44 StartY=90 StartZ=0 EndX=44 EndY=120 EndZ=0
  constraints (20):
    c: Coincident(g3,g2)
    c: Coincident(g3,g1)
    c: PointOnObject(g0,g3)
    c: Radius(g1) = 4
    c: Radius(g2) = 4
    c: Vertical(g3)
    c: Radius(g0) = 11
    c: DistanceY(g2,g1) = 45
    c: Horizontal(g4)
    c: PointOnObject(g4,g-2)
    c: DistanceX(g4,g4) = 44
    c: Coincident(g0,g4)
    c: Symmetric(g1,g2,g4)
    c: Coincident(g5,g0)
    c: PointOnObject(g5,g-3)
    c: Coincident(g6,g0)
    c: Vertical(g6)
    c: Vertical(g5)
    c: Equal(g6,g5)
    c: PointOnObject(g6,g-4)
FEATURE [PartDesign::Pocket] Pocket008
  Length = 7
  Placement = pos=(0,0,0) rot=(1,0,0;1.5708rad)
  Sketch = -> Sketch029
  Type = 0
FEATURE [Sketcher::SketchObject] Sketch030
  ExternalGeometry = -> [Pocket008]
  Placement = pos=(0,0,76) rot=(1,0,0;3.14159rad)
  Support = -> Pocket008 [Face30]
  sketch-geometry (1):
    g0: Circle CenterX=44 CenterY=90 CenterZ=0 NormalX=0 NormalY=0 NormalZ=1 Radius=7
  constraints (2):
    c: Coincident(g0,g-3)
    c: Radius(g0) = 7
FEATURE [PartDesign::Pocket] Pocket009
  Length = 5
  Placement = pos=(0,0,0) rot=(1,0,0;1.5708rad)
  Sketch = -> Sketch030
  Type = 0
FEATURE [Sketcher::SketchObject] Sketch031
  ExternalGeometry = -> [Pocket009]
  Placement = pos=(0,0,24.5) rot=(1,0,0;3.14159rad)
  Support = -> Pocket009 [Face21]
  sketch-geometry (4):
    g0: LineSegment StartX=117 StartY=45 StartZ=0 EndX=77 EndY=45 EndZ=0
    g1: LineSegment StartX=77 StartY=45 StartZ=0 EndX=77 EndY=5 EndZ=0
    g2: LineSegment StartX=77 StartY=5 StartZ=0 EndX=117 EndY=5 EndZ=0
    g3: LineSegment StartX=117 StartY=5 StartZ=0 EndX=117 EndY=45 EndZ=0
  constraints (12):
    c: Coincident(g0,g1)
    c: Coincident(g1,g2)
    c: Coincident(g2,g3)
    c: Coincident(g3,g0)
    c: Horizontal(g0)
    c: Horizontal(g2)
    c: Vertical(g1)
    c: Vertical(g3)
    c: Equal(g1,g2)
    c: DistanceX(g0,g0) = 40
    c: DistanceX(g2,g-5) = 5
    c: DistanceY(g-5,g2) = 5
FEATURE [PartDesign::Pocket] Pocket010
  Length = 40
  Placement = pos=(0,0,0) rot=(1,0,0;1.5708rad)
  Sketch = -> Sketch031
  Type = 0
FEATURE [Part::Box] Box009  label="Cube009"
  Height = 3
  Length = 59
  Placement = pos=(25,-50,0) rot=(0,-1,0;0.523599rad)
  Width = 50
FEATURE [Part::FeaturePython] Clone060  label="Clone of Cube009"  # Draft clone (typed FeaturePython)
  Objects = -> [Box009]
  Placement = pos=(25,0,79) rot=(0.965926,0,-0.258819;3.14159rad)
  Scale = (1,1,1)
FEATURE [Part::MultiFuse] Fusion007
  Shapes = -> [Box009,Pocket010,Clone060]
FEATURE [Part::Fillet] Fillet002
  Base = -> Fusion007
  Edges = 6 edges r=3: [Edge37,Edge39,Edge41,Edge48,Edge75,Edge94]
FEATURE [Part::Fillet] Fillet003  label="BothCarriage"
  Base = -> Fillet002
  Edges = 2 edges r=6: [Edge105,Edge112]
FEATURE [App::DocumentObjectGroup] Group022  label="CarriageBoth"
  Group = -> [Pad015,Pad016,Pad017,Pocket007,Pocket008,Pocket009,Fillet003]
FEATURE [App::DocumentObjectGroup] Group008  label="PrintedParts"
  Group = -> [Pad007,Pad008,Group017,Pad014,Group022]
FEATURE [App::DocumentObjectGroup] Group001  label="Master"
  Group = -> [Group005,Group006,Group008,Group013,Group016,Group018,Group020]
FEATURE [Part::Part2DObjectPython] Line  # Draft 2D object (typed FeaturePython)
  ChamferSize = 0
  Closed = false
  End = (-32.5,165,51)
  FilletRadius = 0
  Length = 103
  MakeFace = true
  Placement = pos=(32.5,3,0) rot=(0,0,1;0rad)
  Points = (2) [(-65,162,154),(-65,162,51)]
  Start = (-32.5,165,154)
  Subdivisions = 0
  expr: Placement.Base.y = XProfile4.Placement.Base.y - 271.5mm
FEATURE [App::DocumentObjectGroup] Group021  label="Laser002"
  Group = -> [Clone057,Line]
FEATURE [Part::Part2DObjectPython] Line001  # Draft 2D object (typed FeaturePython)
  ChamferSize = 0
  Closed = false
  End = (32.5,164.992,50)
  FilletRadius = 0
  Length = 64
  MakeFace = true
  Placement = pos=(-82.5,4,-6) rot=(0,0,1;0rad)
  Points = (2) [(115,160.992,120),(115,160.992,56)]
  Start = (32.5,164.992,114)
  Subdivisions = 0
  expr: Placement.Base.y = XProfile4.Placement.Base.y - 270.5mm
FEATURE [App::DocumentObjectGroup] Group019  label="Spindle002"
  Group = -> [Clone053,Line001]
FEATURE [Part::Box] Box010  label="Cube010"
  Height = 50
  Length = 220
  Placement = pos=(-110,-95,11) rot=(0,0,1;0rad)
  Width = 190
  expr: Placement.Base.y = -Cube010.Width / 2
  expr: Placement.Base.x = -Cube010.Length / 2
  expr: Height = Spreadsheet.WVZ
  expr: Width = Spreadsheet.WVY
  expr: Length = Spreadsheet.WVX
FEATURE [Part::Box] Box011  label="Cube011"
  Height = 10
  Length = 240
  Placement = pos=(-120,-105,0) rot=(0,0,1;0rad)
  Width = 210
  expr: Placement.Base.y = -Cube011.Width / 2
  expr: Placement.Base.x = -Cube011.Length / 2
  expr: Width = Spreadsheet.WVY + 20
  expr: Length = Spreadsheet.WVX + 20
FEATURE [Part::MultiFuse] Fusion008  label="Surface"
  Placement = pos=(0,165,50) rot=(0,0,1;0rad)
  Shapes = -> [Box010,Box011]
  expr: Placement.Base.y = YProfile1.Scale.z / 2
  expr: Placement.Base.x = 0
FEATURE [Spreadsheet::Sheet] Spreadsheet
  cells = E2=Standard Values; B3=Working Volume; C3=X; D3(WVX)=220; E3=220; C4=Y; D4(WVY)=190; E4=190; C5=Z; D5(WVZ)=50; E5=50; C6=Gap Y Distance; D6(Ygap)=25; E6=25
FEATURE [App::DocumentObjectGroup] Group023  label="MillingSurface"
  Group = -> [Fusion008]
FEATURE [Sketcher::SketchObject] Sketch032
  Placement = pos=(0,0,0) rot=(1,0,0;1.5708rad)
  expr: Constraints[23] = (Spreadsheet.WVZ + 70) / 2
  expr: Constraints[20] = Spreadsheet.WVZ + 70
  sketch-geometry (11):
    g0: LineSegment StartX=0 StartY=0 StartZ=0 EndX=25 EndY=0 EndZ=0
    g1: LineSegment StartX=25 StartY=0 StartZ=0 EndX=25 EndY=120 EndZ=0
    g2: LineSegment StartX=25 StartY=120 StartZ=0 EndX=0 EndY=120 EndZ=0
    g3: LineSegment StartX=0 StartY=120 StartZ=0 EndX=0 EndY=0 EndZ=0
    g4: Circle CenterX=12.5 CenterY=12 CenterZ=0 NormalX=0 NormalY=0 NormalZ=1 Radius=7.5
    g5: Circle CenterX=12.5 CenterY=108 CenterZ=0 NormalX=0 NormalY=0 NormalZ=1 Radius=7.5
    g6: Circle CenterX=15.5 CenterY=60 CenterZ=0 NormalX=0 NormalY=0 NormalZ=1 Radius=5
    g7: LineSegment [constr] StartX=12.5 StartY=108 StartZ=0 EndX=12.5 EndY=12 EndZ=0
    g8: LineSegment [constr] StartX=15.5 StartY=60 StartZ=0 EndX=12.5 EndY=60 EndZ=0
    g9: LineSegment [constr] StartX=12.5 StartY=108 StartZ=0 EndX=12.5 EndY=120 EndZ=0
    g10: LineSegment [constr] StartX=12.5 StartY=12 StartZ=0 EndX=12.5 EndY=0 EndZ=0
  constraints (31):
    c: Coincident(g0,g1)
    c: Coincident(g1,g2)
    c: Coincident(g2,g3)
    c: Coincident(g3,g0)
    c: Horizontal(g0)
    c: Horizontal(g2)
    c: Vertical(g1)
    c: Vertical(g3)
    c: Coincident(g0,g-1)
    c: Equal(g5,g4)
    c: Coincident(g7,g5)
    c: Coincident(g7,g4)
    c: Vertical(g7)
    c: Radius(g4) = 7.5
    c: Coincident(g8,g6)
    c: PointOnObject(g8,g7)
    c: Horizontal(g8)
    c: Symmetric(g4,g5,g8)
    c: DistanceX(g8,g8) = 3
    c: Radius(g6) = 5
    c: DistanceY(g3,g3) = 120
    c: DistanceX(g0,g0) = 25
    c: DistanceX(g-1,g4) = 12.5
    c: DistanceY(g-1,g8) = 60
    c: Coincident(g9,g5)
    c: PointOnObject(g9,g2)
    c: Coincident(g10,g4)
    c: PointOnObject(g10,g0)
    c: Vertical(g10)
    c: Perpendicular(g2,g9)
    c: DistanceY(g10,g10) = 12
FEATURE [PartDesign::Pad] Pad018
  Length = 120
  Length2 = 100
  Placement = pos=(0,0,0) rot=(1,0,0;1.5708rad)
  Sketch = -> Sketch032
  Type = 0
FEATURE [Sketcher::SketchObject] Sketch033
  ExternalGeometry = -> [Pad018]
  Placement = pos=(25,0,0) rot=(0.707107,0,0.707107;3.14159rad)
  Support = -> Pad018 [Face2]
  sketch-geometry (6):
    g0: LineSegment StartX=65.5 StartY=0 StartZ=0 EndX=95.5 EndY=0 EndZ=0
    g1: LineSegment StartX=95.5 StartY=0 StartZ=0 EndX=95.5 EndY=50 EndZ=0
    g2: LineSegment StartX=95.5 StartY=50 StartZ=0 EndX=65.5 EndY=50 EndZ=0
    g3: LineSegment StartX=65.5 StartY=50 StartZ=0 EndX=65.5 EndY=0 EndZ=0
    g4: LineSegment [constr] StartX=0 StartY=0 StartZ=0 EndX=65.5 EndY=0 EndZ=0
    g5: LineSegment [constr] StartX=120 StartY=0 StartZ=0 EndX=95.5 EndY=0 EndZ=0
  constraints (16):
    c: Coincident(g0,g1)
    c: Coincident(g1,g2)
    c: Coincident(g2,g3)
    c: Coincident(g3,g0)
    c: Horizontal(g0)
    c: Horizontal(g2)
    c: Vertical(g1)
    c: Vertical(g3)
    c: DistanceY(g1,g1) = 50
    c: DistanceX(g2,g2) = 30
    c: Coincident(g4,g-1)
    c: Coincident(g4,g0)
    c: Coincident(g5,g-3)
    c: Horizontal(g5)
    c: Coincident(g5,g0)
    c: DistanceX(g5,g5) = 24.5
FEATURE [PartDesign::Pad] Pad019
  Length = 97
  Length2 = 100
  Placement = pos=(0,0,0) rot=(1,0,0;1.5708rad)
  Sketch = -> Sketch033
  Type = 0
FEATURE [Sketcher::SketchObject] Sketch034
  Placement = pos=(25,0,0) rot=(0.707107,0,0.707107;3.14159rad)
  Support = -> Pad019 [Face3]
  expr: Constraints[23] = 50 + Spreadsheet.WVZ + 10
  expr: Constraints[19] = 50 + Spreadsheet.WVZ + 20
  sketch-geometry (8):
    g0: LineSegment StartX=0 StartY=120 StartZ=0 EndX=10 EndY=120 EndZ=0
    g1: LineSegment StartX=10 StartY=120 StartZ=0 EndX=10 EndY=60 EndZ=0
    g2: LineSegment StartX=10 StartY=60 StartZ=0 EndX=0 EndY=60 EndZ=0
    g3: LineSegment StartX=0 StartY=60 StartZ=0 EndX=0 EndY=120 EndZ=0
    g4: LineSegment StartX=110 StartY=120 StartZ=0 EndX=120 EndY=120 EndZ=0
    g5: LineSegment StartX=120 StartY=120 StartZ=0 EndX=120 EndY=60 EndZ=0
    g6: LineSegment StartX=120 StartY=60 StartZ=0 EndX=110 EndY=60 EndZ=0
    g7: LineSegment StartX=110 StartY=60 StartZ=0 EndX=110 EndY=120 EndZ=0
  constraints (24):
    c: Coincident(g0,g1)
    c: Coincident(g1,g2)
    c: Coincident(g2,g3)
    c: Coincident(g3,g0)
    c: Horizontal(g0)
    c: Horizontal(g2)
    c: Vertical(g1)
    c: Vertical(g3)
    c: Coincident(g4,g5)
    c: Coincident(g5,g6)
    c: Coincident(g6,g7)
    c: Coincident(g7,g4)
    c: Horizontal(g4)
    c: Horizontal(g6)
    c: Vertical(g5)
    c: Vertical(g7)
    c: DistanceX(g2,g2) = 10
    c: DistanceY(g1,g1) = 60
    c: Equal(g1,g5)
    c: DistanceX(g0,g4) = 120
    c: PointOnObject(g0,g-2)
    c: DistanceY(g0,g4) = 0
    c: DistanceY(g-1,g0) = 120
    c: DistanceX(g0,g4) = 110
FEATURE [PartDesign::Pad] Pad020
  Length = 40
  Length2 = 100
  Placement = pos=(0,0,0) rot=(1,0,0;1.5708rad)
  Sketch = -> Sketch034
  Type = 0
FEATURE [Sketcher::SketchObject] Sketch035
  ExternalGeometry = -> [Pad020]
  Placement = pos=(0,0,0) rot=(1,0,0;3.14159rad)
  Support = -> Pad020 [Face18]
  sketch-geometry (11):
    g0: Circle CenterX=44 CenterY=90 CenterZ=0 NormalX=0 NormalY=0 NormalZ=1 Radius=15
    g1: Circle CenterX=44 CenterY=112.5 CenterZ=0 NormalX=0 NormalY=0 NormalZ=1 Radius=4
    g2: Circle CenterX=44 CenterY=67.5 CenterZ=0 NormalX=0 NormalY=0 NormalZ=1 Radius=4
    g3: Circle CenterX=59.5 CenterY=74.5 CenterZ=0 NormalX=0 NormalY=0 NormalZ=1 Radius=1.5
    g4: Circle CenterX=59.5 CenterY=105.5 CenterZ=0 NormalX=0 NormalY=0 NormalZ=1 Radius=1.5
    g5: Circle CenterX=28.5 CenterY=105.5 CenterZ=0 NormalX=0 NormalY=0 NormalZ=1 Radius=1.5
    g6: Circle CenterX=28.5 CenterY=74.5 CenterZ=0 NormalX=0 NormalY=0 NormalZ=1 Radius=1.5
    g7: LineSegment [constr] StartX=44 StartY=90 StartZ=0 EndX=0 EndY=90 EndZ=0
    g8: LineSegment [constr] StartX=44 StartY=112.5 StartZ=0 EndX=44 EndY=67.5 EndZ=0
    g9: LineSegment [constr] StartX=44 StartY=90 StartZ=0 EndX=44 EndY=120 EndZ=0
    g10: LineSegment [constr] StartX=44 StartY=90 StartZ=0 EndX=44 EndY=60 EndZ=0
  constraints (31):
    c: Coincident(g7,g0)
    c: PointOnObject(g7,g-3)
    c: Horizontal(g7)
    c: DistanceX(g7,g7) = 44
    c: Coincident(g8,g2)
    c: Vertical(g8)
    c: Coincident(g1,g8)
    c: PointOnObject(g0,g8)
    c: Symmetric(g1,g2,g7)
    c: PointOnObject(g9,g7)
    c: PointOnObject(g9,g-4)
    c: Vertical(g9)
    c: Coincident(g10,g9)
    c: PointOnObject(g10,g-5)
    c: Vertical(g10)
    c: Equal(g9,g10)
    c: Symmetric(g5,g4,g8)
    c: Symmetric(g5,g6,g7)
    c: Symmetric(g4,g3,g7)
    c: Symmetric(g3,g6,g8)
    c: Equal(g3,g6)
    c: Equal(g6,g5)
    c: Equal(g5,g4)
    c: Radius(g4) = 1.5
    c: DistanceY(g3,g4) = 31
    c: DistanceX(g6,g3) = 31
    c: Radius(g0) = 15
    c: Equal(g1,g2)
    c: Radius(g1) = 4
    c: Coincident(g9,g0)
    c: DistanceY(g2,g1) = 45
FEATURE [PartDesign::Pocket] Pocket011
  Length = 10
  Placement = pos=(0,0,0) rot=(1,0,0;1.5708rad)
  Sketch = -> Sketch035
  Type = 0
FEATURE [Sketcher::SketchObject] Sketch036
  ExternalGeometry = -> [Pocket011]
  Placement = pos=(0,0,110) rot=(1,0,0;3.14159rad)
  Support = -> Pocket011 [Face25]
  sketch-geometry (7):
    g0: Circle CenterX=44 CenterY=90 CenterZ=0 NormalX=0 NormalY=0 NormalZ=1 Radius=11
    g1: Circle CenterX=44 CenterY=112.5 CenterZ=0 NormalX=0 NormalY=0 NormalZ=1 Radius=4
    g2: Circle CenterX=44 CenterY=67.5 CenterZ=0 NormalX=0 NormalY=0 NormalZ=1 Radius=4
    g3: LineSegment [constr] StartX=44 StartY=67.5 StartZ=0 EndX=44 EndY=112.5 EndZ=0
    g4: LineSegment [constr] StartX=0 StartY=90 StartZ=0 EndX=44 EndY=90 EndZ=0
    g5: LineSegment [constr] StartX=44 StartY=90 StartZ=0 EndX=44 EndY=60 EndZ=0
    g6: LineSegment [constr] StartX=44 StartY=90 StartZ=0 EndX=44 EndY=120 EndZ=0
  constraints (20):
    c: Coincident(g3,g2)
    c: Coincident(g3,g1)
    c: PointOnObject(g0,g3)
    c: Radius(g1) = 4
    c: Radius(g2) = 4
    c: Vertical(g3)
    c: Radius(g0) = 11
    c: DistanceY(g2,g1) = 45
    c: Horizontal(g4)
    c: PointOnObject(g4,g-2)
    c: DistanceX(g4,g4) = 44
    c: Coincident(g0,g4)
    c: Symmetric(g1,g2,g4)
    c: Coincident(g5,g0)
    c: PointOnObject(g5,g-3)
    c: Coincident(g6,g0)
    c: Vertical(g6)
    c: Vertical(g5)
    c: Equal(g6,g5)
    c: PointOnObject(g6,g-4)
FEATURE [PartDesign::Pocket] Pocket012
  Length = 7
  Placement = pos=(0,0,0) rot=(1,0,0;1.5708rad)
  Sketch = -> Sketch036
  Type = 0
FEATURE [Sketcher::SketchObject] Sketch037
  ExternalGeometry = -> [Pocket012]
  Placement = pos=(0,0,117) rot=(1,0,0;3.14159rad)
  Support = -> Pocket012 [Face30]
  sketch-geometry (1):
    g0: Circle CenterX=44 CenterY=90 CenterZ=0 NormalX=0 NormalY=0 NormalZ=1 Radius=7
  constraints (2):
    c: Coincident(g0,g-3)
    c: Radius(g0) = 7
FEATURE [PartDesign::Pocket] Pocket013
  Length = 5
  Placement = pos=(0,0,0) rot=(1,0,0;1.5708rad)
  Sketch = -> Sketch037
  Type = 0
FEATURE [Part::Wedge] Wedge
  Placement = pos=(25,0,60.5) rot=(1,0,0;1.5708rad)
  X2max = 0
  X2min = 0
  Xmax = 48
  Xmin = 0
  Ymax = 24.5
  Ymin = 0
  Z2max = 50
  Z2min = 0
  Zmax = 50
  Zmin = 0
FEATURE [Part::FeaturePython] Clone065  label="Clone of Wedge001"  # Draft clone (typed FeaturePython)
  Objects = -> [Wedge]
  Placement = pos=(30,0,72.6) rot=(1,0,0;1.5708rad)
  Scale = (0.8,1,0.8)
FEATURE [Part::Cut] Cut006
  Base = -> Wedge
  Placement = pos=(0,0,35) rot=(0,0,1;0rad)
  Tool = -> Clone065
  expr: Placement.Base.z = Spreadsheet.WVZ - 15
FEATURE [Part::FeaturePython] Clone066  label="Clone of Cut006"  # Draft clone (typed FeaturePython)
  Objects = -> [Cut006]
  Placement = pos=(0,-50,126) rot=(1,0,0;3.14159rad)
  Scale = (1,1,1)
  expr: Placement.Base.z = Spreadsheet.WVZ + 76
FEATURE [Sketcher::SketchObject] Sketch038
  ExternalGeometry = -> [Pocket013]
  Placement = pos=(0,0,65.5) rot=(1,0,0;3.14159rad)
  Support = -> Pocket013 [Face24]
  sketch-geometry (4):
    g0: LineSegment StartX=77 StartY=45 StartZ=0 EndX=117 EndY=45 EndZ=0
    g1: LineSegment StartX=117 StartY=45 StartZ=0 EndX=117 EndY=5 EndZ=0
    g2: LineSegment StartX=117 StartY=5 StartZ=0 EndX=77 EndY=5 EndZ=0
    g3: LineSegment StartX=77 StartY=5 StartZ=0 EndX=77 EndY=45 EndZ=0
  constraints (12):
    c: Coincident(g0,g1)
    c: Coincident(g1,g2)
    c: Coincident(g2,g3)
    c: Coincident(g3,g0)
    c: Horizontal(g0)
    c: Horizontal(g2)
    c: Vertical(g1)
    c: Vertical(g3)
    c: Equal(g2,g1)
    c: DistanceY(g0,g-4) = 5
    c: DistanceX(g0,g-4) = 5
    c: DistanceY(g-4,g1) = 5
FEATURE [PartDesign::Pocket] Pocket014
  Length = 30
  Placement = pos=(0,0,0) rot=(1,0,0;1.5708rad)
  Sketch = -> Sketch038
  Type = 0
FEATURE [Part::MultiFuse] Fusion009  label="BothCarriageParam"
  Shapes = -> [Cut006,Clone066,Pocket014]
FEATURE [App::DocumentObjectGroup] Group024  label="CarriageBoth001"
  Group = -> [Pad018,Pad019,Pad020,Pocket011,Pocket012,Pocket013,Fusion009]
FEATURE [Part::FeaturePython] Clone067  label="Clone of BothCarriageParam"  # Draft clone (typed FeaturePython)
  Objects = -> [Fusion009]
  Placement = pos=(-57.5,262,241.5) rot=(0.707107,-0.707107,0;3.14159rad)
  Scale = (1,1,1)
  expr: Placement.Base.z = Spreadsheet.WVZ + 191.5
  expr: Placement.Base.y = XProfile4.Placement.Base.y - 12.5mm
FEATURE [App::DocumentObjectGroup] Group009  label="PrintedParts001"
  Group = -> [Part__Mirroring008,Clone048,Clone067]
FEATURE [App::DocumentObjectGroup] Group002  label="Assembly"
  Group = -> [Group003,Group007,Group009,Group011,Group012,Group014,Group015,Group019,Group021,Group023]
